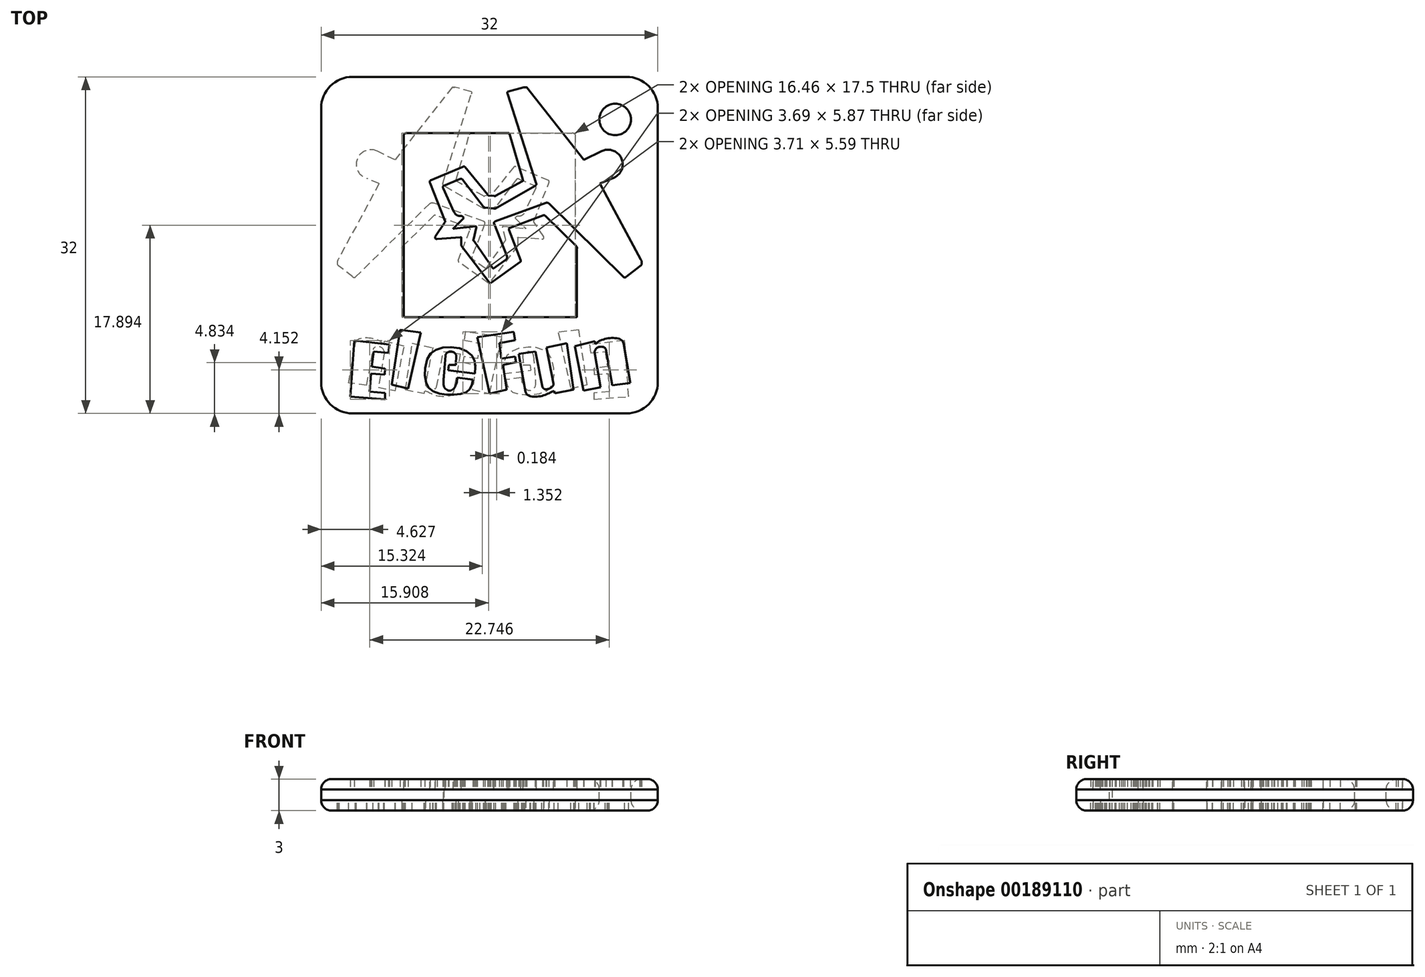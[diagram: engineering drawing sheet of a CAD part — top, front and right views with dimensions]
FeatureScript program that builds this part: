
annotation { "Feature Type Name" : "Feature", "Feature Type Description" : "" }
export const myFeature = defineFeature(function(context is Context, id is Id, definition is map)
    precondition{}
    {
        {
            var Q0;
            Q0=qCreatedBy(makeId("Top.planeOp"),FACE);
            var sketch = newSketch(context, id + "F0", { "sketchPlane" : qUnion([Q0])});
            skLineSegment(sketch, "E0", {"start": v(-15, 0) * mm, "end": v(15, 0) * mm, "construction": true});
            skLineSegment(sketch, "E1", {"start": v(0, 15) * mm, "end": v(0, 0) * mm, "construction": true});
            skLineSegment(sketch, "E2", {"start": v(0, 0) * mm, "end": v(0, -15) * mm, "construction": true});
            skLineSegment(sketch, "E3", {"start": v(1.86, 10.64) * mm, "end": v(-7.86, 10.64) * mm});
            skLineSegment(sketch, "E4", {"start": v(-8.14, 10.51) * mm, "end": v(-8.14, -6.7) * mm});
            skLineSegment(sketch, "E5", {"start": v(-8.02, -6.86) * mm, "end": v(8.23, -6.86) * mm});
            skLineSegment(sketch, "E6", {"start": v(8.32, -6.77) * mm, "end": v(8.32, -0.32) * mm});
            skLineSegment(sketch, "E7", {"start": v(8.28, -0.12) * mm, "end": v(5.28, 2.8) * mm});
            skLineSegment(sketch, "E8", {"start": v(1.92, 1.65) * mm, "end": v(5.12, 2.84) * mm});
            skLineSegment(sketch, "E9", {"start": v(1.74, 14.6) * mm, "end": v(3.24, 15) * mm});
            skLineSegment(sketch, "E10", {"start": v(3.55, 15) * mm, "end": v(8.98, 8.11) * mm});
            skLineSegment(sketch, "E11", {"start": v(8.98, 8.11) * mm, "end": v(10.65, 8.93) * mm});
            skLineSegment(sketch, "E12", {"start": v(10.49, 5.85) * mm, "end": v(11.64, 6.34) * mm});
            skLineSegment(sketch, "E13", {"start": v(10.49, 5.85) * mm, "end": v(14.37, -1.36) * mm});
            skLineSegment(sketch, "E14", {"start": v(13, -3.01) * mm, "end": v(14.27, -2.02) * mm});
            skLineSegment(sketch, "E15", {"start": v(12.74, -3.04) * mm, "end": v(5.65, 3.98) * mm});
            skLineSegment(sketch, "E16", {"start": v(0.54, 2.26) * mm, "end": v(5.35, 4.02) * mm});
            skLineSegment(sketch, "E17", {"start": v(0.45, 2.02) * mm, "end": v(1.66, -1.06) * mm});
            skLineSegment(sketch, "E18", {"start": v(2.97, -1.46) * mm, "end": v(1.87, 1.45) * mm});
            skLineSegment(sketch, "E19", {"start": v(0.4, -2.2) * mm, "end": v(1.6, -1.35) * mm});
            skLineSegment(sketch, "E20", {"start": v(0.28, -2.17) * mm, "end": v(-1.46, 0.35) * mm});
            skLineSegment(sketch, "E21", {"start": v(-1.52, 0.54) * mm, "end": v(-1.27, 1.67) * mm});
            skLineSegment(sketch, "E22", {"start": v(-1.33, 1.8) * mm, "end": v(-3.35, 1.58) * mm});
            skLineSegment(sketch, "E23", {"start": v(-2.43, 2.57) * mm, "end": v(-3.32, 1.7) * mm});
            skLineSegment(sketch, "E24", {"start": v(-2.43, 2.57) * mm, "end": v(-2.63, 2.76) * mm});
            skLineSegment(sketch, "E25", {"start": v(-4.4, 5.43) * mm, "end": v(-3.37, 3.16) * mm});
            skLineSegment(sketch, "E26", {"start": v(-2.79, 0.76) * mm, "end": v(-4.98, 0.6) * mm});
            skLineSegment(sketch, "E27", {"start": v(-5.16, 0.8) * mm, "end": v(-4.24, 2.18) * mm});
            skLineSegment(sketch, "E28", {"start": v(-4.24, 2.33) * mm, "end": v(-5.63, 5.88) * mm});
            skLineSegment(sketch, "E29", {"start": v(-5.63, 6.15) * mm, "end": v(-2.51, 7.46) * mm});
            skLineSegment(sketch, "E30", {"start": v(-2.34, 7.46) * mm, "end": v(-0.18, 4.8) * mm});
            skLineSegment(sketch, "E31", {"start": v(-0.07, 4.7) * mm, "end": v(0.46, 4.67) * mm});
            skLineSegment(sketch, "E32", {"start": v(0.57, 4.67) * mm, "end": v(3.12, 6.06) * mm});
            skLineSegment(sketch, "E33", {"start": v(3.16, 6.27) * mm, "end": v(1.9, 10.52) * mm});
            skLineSegment(sketch, "E34", {"start": v(0.1, -3.6) * mm, "end": v(2.9, -1.6) * mm});
            skLineSegment(sketch, "E35", {"start": v(-2.68, 0.7) * mm, "end": v(-2.7, 0.01) * mm});
            skLineSegment(sketch, "E36", {"start": v(-2.68, -0.05) * mm, "end": v(-0.03, -3.54) * mm});
            skLineSegment(sketch, "E37", {"start": v(-2.76, 6.3) * mm, "end": v(-4.36, 5.63) * mm});
            skLineSegment(sketch, "E38", {"start": v(-2.58, 6.26) * mm, "end": v(-0.6, 3.66) * mm});
            skLineSegment(sketch, "E39", {"start": v(-0.42, 3.58) * mm, "end": v(0.4, 3.49) * mm});
            skLineSegment(sketch, "E40", {"start": v(0.57, 3.49) * mm, "end": v(4.32, 5.63) * mm});
            skLineSegment(sketch, "E41", {"start": v(4.44, 5.9) * mm, "end": v(1.72, 14.38) * mm});
            skArc(sketch, "E42", {"start": v(11.64, 6.34) * mm, "mid": v(12.57, 8.18) * mm, "end": v(10.65, 8.93) * mm});
            skFitSpline(sketch, "E43", {"points": [v(1.74, 14.6) * mm, v(1.69, 14.5) * mm, v(1.72, 14.38) * mm], "startDerivative": vector(-0.14, -0.18) * mm, "endDerivative": vector(0.1, -0.25) * mm});
            skFitSpline(sketch, "E44", {"points": [v(3.24, 15) * mm, v(3.45, 15) * mm, v(3.55, 15) * mm], "startDerivative": vector(0.4, 0.05) * mm, "endDerivative": vector(0.21, -0.06) * mm});
            skFitSpline(sketch, "E45", {"points": [v(14.37, -1.36) * mm, v(14.45, -1.51) * mm, v(14.47, -1.68) * mm, v(14.44, -1.84) * mm, v(14.27, -2.02) * mm], "startDerivative": vector(0.37, -0.61) * mm, "endDerivative": vector(-0.7, -0.58) * mm});
            skFitSpline(sketch, "E46", {"points": [v(13, -3.01) * mm, v(12.88, -3.08) * mm, v(12.74, -3.04) * mm], "startDerivative": vector(-0.22, -0.18) * mm, "endDerivative": vector(-0.3, 0.12) * mm});
            skFitSpline(sketch, "E47", {"points": [v(5.65, 3.98) * mm, v(5.5, 4.03) * mm, v(5.35, 4.02) * mm], "startDerivative": vector(-0.3, 0.13) * mm, "endDerivative": vector(-0.3, -0.04) * mm});
            skArc(sketch, "E48", {"start": v(5.28, 2.8) * mm, "mid": v(5.2, 2.84) * mm, "end": v(5.12, 2.84) * mm});
            skFitSpline(sketch, "E49", {"points": [v(1.92, 1.65) * mm, v(1.86, 1.6) * mm, v(1.85, 1.55) * mm, v(1.87, 1.45) * mm], "startDerivative": vector(-0.21, -0.1) * mm, "endDerivative": vector(0.08, -0.26) * mm});
            skFitSpline(sketch, "E50", {"points": [v(2.97, -1.46) * mm, v(2.98, -1.5) * mm, v(2.97, -1.54) * mm, v(2.95, -1.57) * mm, v(2.9, -1.6) * mm], "startDerivative": vector(0.05, -0.15) * mm, "endDerivative": vector(-0.18, -0.1) * mm});
            skFitSpline(sketch, "E51", {"points": [v(1.66, -1.06) * mm, v(1.66, -1.2) * mm, v(1.6, -1.35) * mm], "startDerivative": vector(0.05, -0.3) * mm, "endDerivative": vector(-0.15, -0.27) * mm});
            skFitSpline(sketch, "E52", {"points": [v(0.4, -2.2) * mm, v(0.35, -2.2) * mm, v(0.28, -2.17) * mm], "startDerivative": vector(-0.13, -0.01) * mm, "endDerivative": vector(-0.12, 0.07) * mm});
            skArc(sketch, "E53", {"start": v(-1.52, 0.54) * mm, "mid": v(-1.52, 0.44) * mm, "end": v(-1.46, 0.35) * mm});
            skFitSpline(sketch, "E54", {"points": [v(-1.27, 1.67) * mm, v(-1.26, 1.7) * mm, v(-1.26, 1.75) * mm, v(-1.27, 1.77) * mm, v(-1.28, 1.79) * mm, v(-1.3, 1.8) * mm, v(-1.33, 1.8) * mm], "startDerivative": vector(0.06, 0.2) * mm, "endDerivative": vector(-0.18, -0.02) * mm});
            skFitSpline(sketch, "E55", {"points": [v(-3.32, 1.7) * mm, v(-3.4, 1.63) * mm, v(-3.44, 1.58) * mm, v(-3.43, 1.57) * mm, v(-3.4, 1.57) * mm, v(-3.35, 1.58) * mm], "startDerivative": vector(-0.28, -0.26) * mm, "endDerivative": vector(0.25, 0.03) * mm});
            skFitSpline(sketch, "E56", {"points": [v(-4.24, 2.18) * mm, v(-4.23, 2.2) * mm, v(-4.21, 2.23) * mm, v(-4.21, 2.25) * mm, v(-4.22, 2.28) * mm, v(-4.23, 2.31) * mm, v(-4.24, 2.33) * mm], "startDerivative": vector(0.05, 0.12) * mm, "endDerivative": vector(-0.05, 0.14) * mm});
            skFitSpline(sketch, "E57", {"points": [v(-2.63, 2.76) * mm, v(-2.75, 2.76) * mm, v(-2.87, 2.76) * mm, v(-3, 2.8) * mm, v(-3.15, 2.89) * mm, v(-3.26, 3) * mm, v(-3.37, 3.16) * mm], "startDerivative": vector(-0.82, 0.01) * mm, "endDerivative": vector(-0.6, 0.94) * mm});
            skFitSpline(sketch, "E58", {"points": [v(-4.4, 5.43) * mm, v(-4.44, 5.55) * mm, v(-4.36, 5.63) * mm], "startDerivative": vector(-0.14, 0.26) * mm, "endDerivative": vector(0.23, 0.16) * mm});
            skFitSpline(sketch, "E59", {"points": [v(-2.76, 6.3) * mm, v(-2.66, 6.3) * mm, v(-2.58, 6.26) * mm], "startDerivative": vector(0.22, 0.03) * mm, "endDerivative": vector(0.16, -0.12) * mm});
            skFitSpline(sketch, "E60", {"points": [v(-0.6, 3.66) * mm, v(-0.52, 3.6) * mm, v(-0.42, 3.58) * mm], "startDerivative": vector(0.15, -0.13) * mm, "endDerivative": vector(0.2, -0.02) * mm});
            skFitSpline(sketch, "E61", {"points": [v(0.4, 3.49) * mm, v(0.5, 3.49) * mm, v(0.57, 3.49) * mm], "startDerivative": vector(0.17, 0) * mm, "endDerivative": vector(0.15, 0) * mm});
            skFitSpline(sketch, "E62", {"points": [v(0.57, 4.67) * mm, v(0.54, 4.66) * mm, v(0.46, 4.67) * mm], "startDerivative": vector(-0.06, -0.02) * mm, "endDerivative": vector(-0.15, 0.02) * mm});
            skFitSpline(sketch, "E63", {"points": [v(-0.07, 4.7) * mm, v(-0.12, 4.73) * mm, v(-0.18, 4.8) * mm], "startDerivative": vector(-0.12, 0.05) * mm, "endDerivative": vector(-0.1, 0.13) * mm});
            skFitSpline(sketch, "E64", {"points": [v(-8.14, 10.51) * mm, v(-8.07, 10.6) * mm, v(-7.95, 10.64) * mm, v(-7.86, 10.64) * mm], "startDerivative": vector(0.18, 0.27) * mm, "endDerivative": vector(0.29, 0) * mm});
            skFitSpline(sketch, "E65", {"points": [v(1.9, 10.52) * mm, v(1.88, 10.6) * mm, v(1.86, 10.64) * mm], "startDerivative": vector(-0.05, 0.15) * mm, "endDerivative": vector(-0.04, 0.1) * mm});
            skFitSpline(sketch, "E66", {"points": [v(4.44, 5.9) * mm, v(4.45, 5.84) * mm, v(4.45, 5.77) * mm, v(4.43, 5.72) * mm, v(4.4, 5.69) * mm, v(4.32, 5.63) * mm], "startDerivative": vector(0.07, -0.32) * mm, "endDerivative": vector(-0.37, -0.23) * mm});
            skFitSpline(sketch, "E67", {"points": [v(3.12, 6.06) * mm, v(3.16, 6.1) * mm, v(3.18, 6.13) * mm, v(3.18, 6.17) * mm, v(3.16, 6.27) * mm], "startDerivative": vector(0.2, 0.13) * mm, "endDerivative": vector(-0.1, 0.32) * mm});
            skFitSpline(sketch, "E68", {"points": [v(-4.98, 0.6) * mm, v(-5.04, 0.6) * mm, v(-5.1, 0.6) * mm, v(-5.13, 0.63) * mm, v(-5.16, 0.66) * mm, v(-5.17, 0.7) * mm, v(-5.17, 0.74) * mm, v(-5.17, 0.78) * mm, v(-5.16, 0.8) * mm], "startDerivative": vector(-0.4, 0) * mm, "endDerivative": vector(0.04, 0.24) * mm});
            skFitSpline(sketch, "E69", {"points": [v(-2.68, 0.7) * mm, v(-2.68, 0.73) * mm, v(-2.69, 0.74) * mm, v(-2.7, 0.75) * mm, v(-2.72, 0.76) * mm, v(-2.74, 0.76) * mm, v(-2.79, 0.76) * mm], "startDerivative": vector(-0.02, 0.12) * mm, "endDerivative": vector(-0.22, -0.02) * mm});
            skFitSpline(sketch, "E70", {"points": [v(-2.68, -0.05) * mm, v(-2.7, -0.03) * mm, v(-2.7, 0.01) * mm], "startDerivative": vector(-0.02, 0.05) * mm, "endDerivative": vector(0, 0.08) * mm});
            skFitSpline(sketch, "E71", {"points": [v(0.1, -3.6) * mm, v(0.08, -3.6) * mm, v(0.04, -3.6) * mm, v(0, -3.6) * mm, v(-0.03, -3.54) * mm], "startDerivative": vector(-0.1, -0.1) * mm, "endDerivative": vector(-0.12, 0.19) * mm});
            skFitSpline(sketch, "E72", {"points": [v(-8.14, -6.7) * mm, v(-8.14, -6.74) * mm, v(-8.13, -6.78) * mm, v(-8.1, -6.82) * mm, v(-8.08, -6.84) * mm, v(-8.04, -6.86) * mm, v(-8.02, -6.86) * mm], "startDerivative": vector(-0.01, -0.18) * mm, "endDerivative": vector(0.15, 0.01) * mm});
            skFitSpline(sketch, "E73", {"points": [v(8.32, -6.77) * mm, v(8.3, -6.83) * mm, v(8.23, -6.86) * mm], "startDerivative": vector(-0.01, -0.15) * mm, "endDerivative": vector(-0.16, -0.02) * mm});
            skFitSpline(sketch, "E74", {"points": [v(8.32, -0.32) * mm, v(8.32, -0.22) * mm, v(8.28, -0.12) * mm], "startDerivative": vector(0.02, 0.2) * mm, "endDerivative": vector(-0.1, 0.2) * mm});
            skFitSpline(sketch, "E75", {"points": [v(-5.63, 5.88) * mm, v(-5.68, 6.02) * mm, v(-5.63, 6.15) * mm], "startDerivative": vector(-0.15, 0.28) * mm, "endDerivative": vector(0.15, 0.27) * mm});
            skFitSpline(sketch, "E76", {"points": [v(-2.51, 7.46) * mm, v(-2.42, 7.48) * mm, v(-2.34, 7.46) * mm], "startDerivative": vector(0.18, 0.06) * mm, "endDerivative": vector(0.15, -0.07) * mm});
            skLineSegment(sketch, "E77", {"start": v(-9.52, -9.44) * mm, "end": v(-9.6, -10.25) * mm});
            skLineSegment(sketch, "E78", {"start": v(-9.6, -10.25) * mm, "end": v(-11, -10.11) * mm});
            skLineSegment(sketch, "E79", {"start": v(-11, -10.11) * mm, "end": v(-11.2, -11.55) * mm});
            skLineSegment(sketch, "E80", {"start": v(-11.2, -11.55) * mm, "end": v(-9.91, -11.72) * mm});
            skLineSegment(sketch, "E81", {"start": v(-9.91, -11.72) * mm, "end": v(-9.96, -12.3) * mm});
            skLineSegment(sketch, "E82", {"start": v(-9.96, -12.3) * mm, "end": v(-11.25, -12.2) * mm});
            skLineSegment(sketch, "E83", {"start": v(-11.25, -12.2) * mm, "end": v(-11.4, -13.92) * mm});
            skLineSegment(sketch, "E84", {"start": v(-11.4, -13.92) * mm, "end": v(-9.9, -14.05) * mm});
            skLineSegment(sketch, "E85", {"start": v(-9.9, -14.05) * mm, "end": v(-9.9, -14.64) * mm});
            skLineSegment(sketch, "E86", {"start": v(-9.9, -14.64) * mm, "end": v(-13.23, -14.4) * mm});
            skLineSegment(sketch, "E87", {"start": v(-13.23, -14.4) * mm, "end": v(-12.84, -9.05) * mm});
            skLineSegment(sketch, "E88", {"start": v(-12.84, -9.05) * mm, "end": v(-9.52, -9.44) * mm});
            skLineSegment(sketch, "E89", {"start": v(-8.48, -8.05) * mm, "end": v(-6.54, -8.29) * mm});
            skLineSegment(sketch, "E90", {"start": v(-6.54, -8.29) * mm, "end": v(-7.72, -13.63) * mm});
            skLineSegment(sketch, "E91", {"start": v(-7.72, -13.63) * mm, "end": v(-9.28, -13.26) * mm});
            skLineSegment(sketch, "E92", {"start": v(-9.28, -13.26) * mm, "end": v(-8.48, -8.05) * mm});
            skLineSegment(sketch, "E93", {"start": v(-3.17, -10.43) * mm, "end": v(-3.2, -11.4) * mm});
            skLineSegment(sketch, "E94", {"start": v(-3.2, -11.4) * mm, "end": v(-3.87, -11.4) * mm});
            skFitSpline(sketch, "E95", {"points": [v(-4.2, -10.53) * mm, v(-4.15, -10.37) * mm, v(-4.02, -10.22) * mm, v(-3.84, -10.13) * mm, v(-3.58, -10.13) * mm, v(-3.37, -10.2) * mm, v(-3.24, -10.32) * mm, v(-3.17, -10.43) * mm], "startDerivative": vector(0.24, 1.24) * mm, "endDerivative": vector(0.53, -0.96) * mm});
            skLineSegment(sketch, "E96", {"start": v(-1.38, -12.22) * mm, "end": v(-3.93, -11.9) * mm});
            skLineSegment(sketch, "E97", {"start": v(-3.06, -12.6) * mm, "end": v(-1.58, -12.8) * mm});
            skFitSpline(sketch, "E98", {"points": [v(-1.58, -12.8) * mm, v(-1.61, -13.06) * mm, v(-1.68, -13.28) * mm, v(-1.78, -13.5) * mm, v(-1.9, -13.7) * mm, v(-2.08, -13.9) * mm, v(-2.35, -14.05) * mm, v(-2.72, -14.14) * mm, v(-3.17, -14.2) * mm, v(-3.7, -14.2) * mm, v(-4.27, -14.19) * mm, v(-4.76, -14.11) * mm, v(-5.25, -13.94) * mm, v(-5.5, -13.78) * mm, v(-5.75, -13.59) * mm, v(-5.94, -13.25) * mm, v(-6.09, -12.8) * mm, v(-6.14, -12.22) * mm, v(-6.12, -11.7) * mm, v(-5.92, -10.84) * mm, v(-5.69, -10.42) * mm, v(-5.37, -10.12) * mm, v(-4.96, -9.9) * mm, v(-4.42, -9.73) * mm, v(-3.73, -9.7) * mm, v(-2.96, -9.77) * mm, v(-2.33, -9.98) * mm, v(-1.87, -10.28) * mm, v(-1.58, -10.62) * mm, v(-1.4, -10.98) * mm, v(-1.35, -11.33) * mm, v(-1.34, -11.71) * mm, v(-1.38, -12.22) * mm], "startDerivative": vector(-0.95, -11.32) * mm, "endDerivative": vector(-1.59, -15.64) * mm});
            skLineSegment(sketch, "E99", {"start": v(1.62, -13.75) * mm, "end": v(0, -14.1) * mm});
            skLineSegment(sketch, "E100", {"start": v(0, -14.1) * mm, "end": v(-1.17, -8.73) * mm});
            skLineSegment(sketch, "E101", {"start": v(-1.17, -8.73) * mm, "end": v(2.3, -8.23) * mm});
            skLineSegment(sketch, "E102", {"start": v(2.3, -8.23) * mm, "end": v(2.42, -9.03) * mm});
            skLineSegment(sketch, "E103", {"start": v(2.42, -9.03) * mm, "end": v(0.92, -9.32) * mm});
            skLineSegment(sketch, "E104", {"start": v(0.92, -9.32) * mm, "end": v(1.14, -10.78) * mm});
            skLineSegment(sketch, "E105", {"start": v(1.14, -10.78) * mm, "end": v(2.44, -10.6) * mm});
            skLineSegment(sketch, "E106", {"start": v(2.44, -10.6) * mm, "end": v(2.52, -11.14) * mm});
            skLineSegment(sketch, "E107", {"start": v(2.52, -11.14) * mm, "end": v(1.28, -11.38) * mm});
            skLineSegment(sketch, "E108", {"start": v(1.28, -11.38) * mm, "end": v(1.62, -13.75) * mm});
            skLineSegment(sketch, "E109", {"start": v(7.98, -13.75) * mm, "end": v(6.2, -14.08) * mm});
            skLineSegment(sketch, "E110", {"start": v(6.2, -14.08) * mm, "end": v(6.13, -13.86) * mm});
            skLineSegment(sketch, "E111", {"start": v(7.98, -13.75) * mm, "end": v(7.34, -9.32) * mm});
            skLineSegment(sketch, "E112", {"start": v(7.34, -9.32) * mm, "end": v(5.4, -9.74) * mm});
            skLineSegment(sketch, "E113", {"start": v(5.4, -9.74) * mm, "end": v(6.08, -13.15) * mm});
            skLineSegment(sketch, "E114", {"start": v(5.02, -13.5) * mm, "end": v(4.37, -10.12) * mm});
            skLineSegment(sketch, "E115", {"start": v(4.37, -10.12) * mm, "end": v(2.77, -10.33) * mm});
            skLineSegment(sketch, "E116", {"start": v(2.77, -10.33) * mm, "end": v(3.4, -13.9) * mm});
            skFitSpline(sketch, "E117", {"points": [v(3.4, -13.9) * mm, v(3.49, -14.1) * mm, v(3.68, -14.27) * mm, v(3.94, -14.38) * mm, v(4.27, -14.4) * mm, v(4.69, -14.38) * mm, v(5.07, -14.3) * mm, v(5.38, -14.2) * mm, v(5.68, -14.07) * mm, v(5.87, -13.97) * mm, v(6, -13.9) * mm, v(6.13, -13.86) * mm], "startDerivative": vector(0.77, -2.56) * mm, "endDerivative": vector(2.11, 0.24) * mm});
            skFitSpline(sketch, "E118", {"points": [v(6.08, -13.15) * mm, v(6.08, -13.3) * mm, v(5.99, -13.43) * mm, v(5.86, -13.54) * mm, v(5.67, -13.64) * mm, v(5.51, -13.68) * mm, v(5.33, -13.7) * mm, v(5.2, -13.66) * mm, v(5.11, -13.6) * mm, v(5.02, -13.5) * mm], "startDerivative": vector(0.2, -1.45) * mm, "endDerivative": vector(-0.8, 1.2) * mm});
            skLineSegment(sketch, "E119", {"start": v(10.55, -13.52) * mm, "end": v(8.95, -13.82) * mm});
            skLineSegment(sketch, "E120", {"start": v(8.95, -13.82) * mm, "end": v(8.1, -9.6) * mm});
            skLineSegment(sketch, "E121", {"start": v(8.1, -9.6) * mm, "end": v(10.02, -9.13) * mm});
            skLineSegment(sketch, "E122", {"start": v(10.02, -9.13) * mm, "end": v(10.05, -9.43) * mm});
            skLineSegment(sketch, "E123", {"start": v(9.98, -10.17) * mm, "end": v(10.55, -13.52) * mm});
            skLineSegment(sketch, "E124", {"start": v(11.66, -13.3) * mm, "end": v(11.06, -9.93) * mm});
            skLineSegment(sketch, "E125", {"start": v(11.66, -13.3) * mm, "end": v(13.38, -13.1) * mm});
            skLineSegment(sketch, "E126", {"start": v(13.38, -13.1) * mm, "end": v(12.75, -9.36) * mm});
            skPoint(sketch, "E127.1.internal.snap0", {"position": v(10.04, -9.28) * mm});
            skFitSpline(sketch, "E127", {"points": [v(9.98, -10.17) * mm, v(10.04, -9.98) * mm, v(10.15, -9.81) * mm, v(10.35, -9.7) * mm, v(10.58, -9.65) * mm, v(10.8, -9.68) * mm, v(10.92, -9.73) * mm, v(11, -9.8) * mm, v(11.06, -9.93) * mm], "startDerivative": vector(0.35, 1.5) * mm, "endDerivative": vector(0.4, -1.27) * mm});
            skFitSpline(sketch, "E128", {"points": [v(10.05, -9.43) * mm, v(10.22, -9.26) * mm, v(10.4, -9.14) * mm, v(10.7, -9) * mm, v(11.1, -8.88) * mm, v(11.5, -8.83) * mm, v(11.9, -8.84) * mm, v(12.26, -8.88) * mm, v(12.5, -8.98) * mm, v(12.65, -9.13) * mm, v(12.7, -9.24) * mm, v(12.75, -9.36) * mm], "startDerivative": vector(2, 2.1) * mm, "endDerivative": vector(0.8, -1.94) * mm});
            skFitSpline(sketch, "E129", {"points": [v(-4.1, -11.87) * mm, v(-4.2, -12.04) * mm, v(-4.27, -12.28) * mm, v(-4.35, -12.58) * mm, v(-4.37, -12.86) * mm, v(-4.38, -13.16) * mm, v(-4.32, -13.48) * mm, v(-4.14, -13.7) * mm, v(-3.92, -13.8) * mm, v(-3.7, -13.82) * mm, v(-3.5, -13.73) * mm, v(-3.35, -13.58) * mm, v(-3.22, -13.37) * mm, v(-3.14, -13.13) * mm, v(-3.1, -12.91) * mm, v(-3.06, -12.6) * mm], "startDerivative": vector(-1.74, -2.77) * mm, "endDerivative": vector(0.4, 4.42) * mm});
            skFitSpline(sketch, "E130", {"points": [v(0.45, 2.02) * mm, v(0.43, 2.1) * mm, v(0.45, 2.18) * mm, v(0.54, 2.26) * mm], "startDerivative": vector(-0.1, 0.25) * mm, "endDerivative": vector(0.3, 0.19) * mm});
            skLineSegment(sketch, "E131", {"start": v(8.89, 15) * mm, "end": v(15, 8.89) * mm, "construction": true});
            skCircle(sketch, "E132", {"center": v(11.94, 11.94) * mm, "radius": 1.5 * mm});
            skLineSegment(sketch, "E133.bottom", {"start": v(-13, 16) * mm, "end": v(13, 16) * mm});
            skLineSegment(sketch, "E133.top", {"start": v(-13, -16) * mm, "end": v(13, -16) * mm});
            skLineSegment(sketch, "E133.left", {"start": v(-16, 13) * mm, "end": v(-16, -13) * mm});
            skLineSegment(sketch, "E133.right", {"start": v(16, 13) * mm, "end": v(16, -13) * mm});
            skLineSegment(sketch, "E134", {"start": v(-16, 0) * mm, "end": v(16, 0) * mm, "construction": true});
            skLineSegment(sketch, "E135", {"start": v(0, 16) * mm, "end": v(0, -16) * mm, "construction": true});
            skLineSegment(sketch, "E136", {"start": v(0, 0) * mm, "end": v(0, -16) * mm, "construction": true});
            skLineSegment(sketch, "E137", {"start": v(0, -16) * mm, "end": v(0, 0) * mm, "construction": true});
            skLineSegment(sketch, "E138", {"start": v(0, 16) * mm, "end": v(0, 0) * mm, "construction": true});
            skPoint(sketch, "E139.visualSharp", {"position": v(-16, 16) * mm});
            skArc(sketch, "E139.filletArc", {"start": v(-13, 16) * mm, "mid": v(-15.12, 15.12) * mm, "end": v(-16, 13) * mm});
            skPoint(sketch, "E140.visualSharp", {"position": v(16, 16) * mm});
            skArc(sketch, "E140.filletArc", {"start": v(16, 13) * mm, "mid": v(15.12, 15.12) * mm, "end": v(13, 16) * mm});
            skPoint(sketch, "E141.visualSharp", {"position": v(16, -16) * mm});
            skArc(sketch, "E141.filletArc", {"start": v(13, -16) * mm, "mid": v(15.12, -15.12) * mm, "end": v(16, -13) * mm});
            skPoint(sketch, "E142.visualSharp", {"position": v(-16, -16) * mm});
            skArc(sketch, "E142.filletArc", {"start": v(-16, -13) * mm, "mid": v(-15.12, -15.12) * mm, "end": v(-13, -16) * mm});
            skLineSegment(sketch, "E143", {"start": v(-4.19, -10.48) * mm, "end": v(-4.37, -12.86) * mm});
            skLineSegment(sketch, "E144", {"start": v(-3.87, -11.4) * mm, "end": v(-3.93, -11.9) * mm});
            skSolve(sketch);
        }
        {
            var Q0;
            Q0=makeQuery(id+"F0.imprint","IMPRINT",FACE,{"disambiguationData":[TD([[makeQuery(id+"F0.imprint","IMPRINT",EDGE,{"derivedFrom":sQuery(id+"F0.wireOp",EDGE,"E9")}),-1.0]])]});
            var Q1;
            Q1=makeQuery(id+"F0.imprint","IMPRINT",FACE,{"disambiguationData":[TD([[makeQuery(id+"F0.imprint","IMPRINT",EDGE,{"derivedFrom":sQuery(id+"F0.wireOp",EDGE,"E132")}),1.0]])]});
            var Q2;
            Q2=makeQuery(id+"F0.imprint","IMPRINT",FACE,{"disambiguationData":[TD([[makeQuery(id+"F0.imprint","IMPRINT",EDGE,{"derivedFrom":sQuery(id+"F0.wireOp",EDGE,"E119")}),-1.0]])]});
            var Q3;
            Q3=makeQuery(id+"F0.imprint","IMPRINT",FACE,{"disambiguationData":[TD([[makeQuery(id+"F0.imprint","IMPRINT",EDGE,{"derivedFrom":sQuery(id+"F0.wireOp",EDGE,"E93")}),1.0]])]});
            var Q4;
            Q4=makeQuery(id+"F0.imprint","IMPRINT",FACE,{"disambiguationData":[TD([[makeQuery(id+"F0.imprint","IMPRINT",EDGE,{"derivedFrom":sQuery(id+"F0.wireOp",EDGE,"E3")}),1.0]])]});
            var Q5;
            Q5=makeQuery(id+"F0.imprint","IMPRINT",FACE,{"disambiguationData":[TD([[makeQuery(id+"F0.imprint","IMPRINT",EDGE,{"derivedFrom":sQuery(id+"F0.wireOp",EDGE,"E3")}),-1.0]])]});
            var Q6;
            Q6=makeQuery(id+"F0.imprint","IMPRINT",FACE,{"disambiguationData":[TD([[makeQuery(id+"F0.imprint","IMPRINT",EDGE,{"derivedFrom":sQuery(id+"F0.wireOp",EDGE,"E89")}),-1.0]])]});
            var Q7;
            Q7=makeQuery(id+"F0.imprint","IMPRINT",FACE,{"disambiguationData":[TD([[makeQuery(id+"F0.imprint","IMPRINT",EDGE,{"derivedFrom":sQuery(id+"F0.wireOp",EDGE,"E99")}),-1.0]])]});
            var Q8;
            Q8=makeQuery(id+"F0.imprint","IMPRINT",FACE,{"disambiguationData":[TD([[makeQuery(id+"F0.imprint","IMPRINT",EDGE,{"derivedFrom":sQuery(id+"F0.wireOp",EDGE,"E109")}),-1.0]])]});
            var Q9;
            Q9=makeQuery(id+"F0.imprint","IMPRINT",FACE,{"disambiguationData":[TD([[makeQuery(id+"F0.imprint","IMPRINT",EDGE,{"derivedFrom":sQuery(id+"F0.wireOp",EDGE,"E77")}),-1.0]])]});
            extrude(context, id + "F1", {"entities" : qUnion([Q0, Q1, Q2, Q3, Q4, Q5, Q6, Q7, Q8, Q9]), "oppositeDirection" : true, "depth" : 1 * mm});
        }
        {
            var Q0;
            Q0=makeQuery(id+"F0.imprint","IMPRINT",FACE,{"disambiguationData":[TD([[makeQuery(id+"F0.imprint","IMPRINT",EDGE,{"derivedFrom":sQuery(id+"F0.wireOp",EDGE,"E3")}),-1.0]])]});
            extrude(context, id + "F2", {"entities" : qUnion([Q0]), "depth" : 1 * mm});
        }
        {
            var Q0;
            Q0=makeQuery(id+"F1.opExtrude","CAP_FACE",FACE,{"disambiguationData":[OSD([sQuery(id+"F0.wireOp",EDGE,"E133.bottom"),sQuery(id+"F0.wireOp",EDGE,"E133.top"),sQuery(id+"F0.wireOp",EDGE,"E133.left"),sQuery(id+"F0.wireOp",EDGE,"E133.right"),sQuery(id+"F0.wireOp",EDGE,"E139.filletArc"),sQuery(id+"F0.wireOp",EDGE,"E140.filletArc"),sQuery(id+"F0.wireOp",EDGE,"E141.filletArc"),sQuery(id+"F0.wireOp",EDGE,"E142.filletArc")])],"isStart":false});
            var sketch = newSketch(context, id + "F3", { "sketchPlane" : qUnion([Q0])});
            skLineSegment(sketch, "E145", {"start": v(-15.73, 2.68) * mm, "end": v(14.27, 2.68) * mm, "construction": true});
            skLineSegment(sketch, "E146", {"start": v(-0.73, 17.68) * mm, "end": v(-0.73, 2.68) * mm, "construction": true});
            skLineSegment(sketch, "E147", {"start": v(-0.73, 2.68) * mm, "end": v(-0.73, -12.32) * mm, "construction": true});
            skLineSegment(sketch, "E148", {"start": v(1.13, 13.33) * mm, "end": v(-8.59, 13.33) * mm});
            skLineSegment(sketch, "E149", {"start": v(-8.87, 13.2) * mm, "end": v(-8.87, -4.03) * mm});
            skLineSegment(sketch, "E150", {"start": v(-8.75, -4.17) * mm, "end": v(7.5, -4.17) * mm});
            skLineSegment(sketch, "E151", {"start": v(7.58, -4.09) * mm, "end": v(7.58, 2.37) * mm});
            skLineSegment(sketch, "E152", {"start": v(7.54, 2.56) * mm, "end": v(4.54, 5.48) * mm});
            skLineSegment(sketch, "E153", {"start": v(1.19, 4.33) * mm, "end": v(4.4, 5.53) * mm});
            skLineSegment(sketch, "E154", {"start": v(1, 17.28) * mm, "end": v(2.5, 17.67) * mm});
            skLineSegment(sketch, "E155", {"start": v(2.82, 17.67) * mm, "end": v(8.25, 10.8) * mm});
            skLineSegment(sketch, "E156", {"start": v(8.25, 10.8) * mm, "end": v(9.91, 11.61) * mm});
            skLineSegment(sketch, "E157", {"start": v(9.75, 8.54) * mm, "end": v(10.9, 9.02) * mm});
            skLineSegment(sketch, "E158", {"start": v(9.75, 8.54) * mm, "end": v(13.64, 1.32) * mm});
            skLineSegment(sketch, "E159", {"start": v(12.27, -0.33) * mm, "end": v(13.54, 0.67) * mm});
            skLineSegment(sketch, "E160", {"start": v(12, -0.36) * mm, "end": v(4.92, 6.66) * mm});
            skLineSegment(sketch, "E161", {"start": v(-0.19, 4.94) * mm, "end": v(4.62, 6.7) * mm});
            skLineSegment(sketch, "E162", {"start": v(-0.28, 4.7) * mm, "end": v(0.92, 1.62) * mm});
            skLineSegment(sketch, "E163", {"start": v(2.24, 1.22) * mm, "end": v(1.13, 4.14) * mm});
            skLineSegment(sketch, "E164", {"start": v(-0.33, 0.48) * mm, "end": v(0.87, 1.33) * mm});
            skLineSegment(sketch, "E165", {"start": v(-0.45, 0.51) * mm, "end": v(-2.2, 3.04) * mm});
            skLineSegment(sketch, "E166", {"start": v(-2.26, 3.23) * mm, "end": v(-2, 4.35) * mm});
            skLineSegment(sketch, "E167", {"start": v(-2.06, 4.48) * mm, "end": v(-4.08, 4.26) * mm});
            skLineSegment(sketch, "E168", {"start": v(-3.16, 5.25) * mm, "end": v(-4.06, 4.39) * mm});
            skLineSegment(sketch, "E169", {"start": v(-3.16, 5.25) * mm, "end": v(-3.36, 5.45) * mm});
            skLineSegment(sketch, "E170", {"start": v(-5.13, 8.1) * mm, "end": v(-4.1, 5.85) * mm});
            skLineSegment(sketch, "E171", {"start": v(-3.52, 3.44) * mm, "end": v(-5.71, 3.28) * mm});
            skLineSegment(sketch, "E172", {"start": v(-5.9, 3.48) * mm, "end": v(-4.97, 4.86) * mm});
            skLineSegment(sketch, "E173", {"start": v(-4.97, 5.02) * mm, "end": v(-6.36, 8.56) * mm});
            skLineSegment(sketch, "E174", {"start": v(-6.36, 8.84) * mm, "end": v(-3.24, 10.14) * mm});
            skLineSegment(sketch, "E175", {"start": v(-3.08, 10.14) * mm, "end": v(-0.91, 7.48) * mm});
            skLineSegment(sketch, "E176", {"start": v(-0.8, 7.39) * mm, "end": v(-0.27, 7.35) * mm});
            skLineSegment(sketch, "E177", {"start": v(-0.16, 7.35) * mm, "end": v(2.39, 8.75) * mm});
            skLineSegment(sketch, "E178", {"start": v(2.43, 8.95) * mm, "end": v(1.18, 13.2) * mm});
            skLineSegment(sketch, "E179", {"start": v(-0.63, -0.9) * mm, "end": v(2.17, 1.08) * mm});
            skLineSegment(sketch, "E180", {"start": v(-3.4, 3.4) * mm, "end": v(-3.42, 2.7) * mm});
            skLineSegment(sketch, "E181", {"start": v(-3.42, 2.63) * mm, "end": v(-0.76, -0.86) * mm});
            skLineSegment(sketch, "E182", {"start": v(-3.5, 8.99) * mm, "end": v(-5.09, 8.32) * mm});
            skLineSegment(sketch, "E183", {"start": v(-3.3, 8.94) * mm, "end": v(-1.33, 6.34) * mm});
            skLineSegment(sketch, "E184", {"start": v(-1.15, 6.26) * mm, "end": v(-0.32, 6.17) * mm});
            skLineSegment(sketch, "E185", {"start": v(-0.16, 6.17) * mm, "end": v(3.59, 8.32) * mm});
            skLineSegment(sketch, "E186", {"start": v(3.7, 8.58) * mm, "end": v(0.99, 17.06) * mm});
            skArc(sketch, "E187", {"start": v(10.9, 9.02) * mm, "mid": v(11.84, 10.86) * mm, "end": v(9.91, 11.61) * mm});
            skFitSpline(sketch, "E188", {"points": [v(1, 17.28) * mm, v(0.96, 17.19) * mm, v(0.99, 17.06) * mm], "startDerivative": vector(-0.14, -0.18) * mm, "endDerivative": vector(0.1, -0.25) * mm});
            skFitSpline(sketch, "E189", {"points": [v(2.5, 17.67) * mm, v(2.72, 17.7) * mm, v(2.82, 17.67) * mm], "startDerivative": vector(0.4, 0.05) * mm, "endDerivative": vector(0.21, -0.06) * mm});
            skFitSpline(sketch, "E190", {"points": [v(13.64, 1.32) * mm, v(13.72, 1.17) * mm, v(13.74, 1) * mm, v(13.71, 0.84) * mm, v(13.54, 0.67) * mm], "startDerivative": vector(0.37, -0.61) * mm, "endDerivative": vector(-0.7, -0.58) * mm});
            skFitSpline(sketch, "E191", {"points": [v(12.27, -0.33) * mm, v(12.15, -0.4) * mm, v(12, -0.36) * mm], "startDerivative": vector(-0.22, -0.18) * mm, "endDerivative": vector(-0.3, 0.12) * mm});
            skFitSpline(sketch, "E192", {"points": [v(4.92, 6.66) * mm, v(4.77, 6.71) * mm, v(4.62, 6.7) * mm], "startDerivative": vector(-0.3, 0.13) * mm, "endDerivative": vector(-0.3, -0.04) * mm});
            skArc(sketch, "E193", {"start": v(4.54, 5.48) * mm, "mid": v(4.47, 5.52) * mm, "end": v(4.4, 5.53) * mm});
            skFitSpline(sketch, "E194", {"points": [v(1.19, 4.33) * mm, v(1.13, 4.3) * mm, v(1.11, 4.23) * mm, v(1.13, 4.14) * mm], "startDerivative": vector(-0.21, -0.1) * mm, "endDerivative": vector(0.08, -0.26) * mm});
            skFitSpline(sketch, "E195", {"points": [v(2.24, 1.22) * mm, v(2.25, 1.19) * mm, v(2.24, 1.15) * mm, v(2.22, 1.1) * mm, v(2.17, 1.08) * mm], "startDerivative": vector(0.05, -0.15) * mm, "endDerivative": vector(-0.18, -0.1) * mm});
            skFitSpline(sketch, "E196", {"points": [v(0.92, 1.62) * mm, v(0.93, 1.47) * mm, v(0.87, 1.33) * mm], "startDerivative": vector(0.05, -0.3) * mm, "endDerivative": vector(-0.15, -0.27) * mm});
            skFitSpline(sketch, "E197", {"points": [v(-0.33, 0.48) * mm, v(-0.39, 0.48) * mm, v(-0.45, 0.51) * mm], "startDerivative": vector(-0.13, -0.01) * mm, "endDerivative": vector(-0.12, 0.07) * mm});
            skArc(sketch, "E198", {"start": v(-2.26, 3.23) * mm, "mid": v(-2.25, 3.12) * mm, "end": v(-2.2, 3.04) * mm});
            skFitSpline(sketch, "E199", {"points": [v(-2, 4.35) * mm, v(-2, 4.4) * mm, v(-2, 4.43) * mm, v(-2, 4.45) * mm, v(-2.01, 4.47) * mm, v(-2.03, 4.48) * mm, v(-2.06, 4.48) * mm], "startDerivative": vector(0.06, 0.2) * mm, "endDerivative": vector(-0.18, -0.02) * mm});
            skFitSpline(sketch, "E200", {"points": [v(-4.06, 4.39) * mm, v(-4.14, 4.31) * mm, v(-4.17, 4.27) * mm, v(-4.16, 4.25) * mm, v(-4.13, 4.25) * mm, v(-4.08, 4.26) * mm], "startDerivative": vector(-0.28, -0.26) * mm, "endDerivative": vector(0.25, 0.03) * mm});
            skFitSpline(sketch, "E201", {"points": [v(-4.97, 4.86) * mm, v(-4.96, 4.88) * mm, v(-4.95, 4.9) * mm, v(-4.95, 4.93) * mm, v(-4.95, 4.97) * mm, v(-4.96, 5) * mm, v(-4.97, 5.02) * mm], "startDerivative": vector(0.05, 0.12) * mm, "endDerivative": vector(-0.05, 0.14) * mm});
            skFitSpline(sketch, "E202", {"points": [v(-3.36, 5.45) * mm, v(-3.48, 5.45) * mm, v(-3.6, 5.45) * mm, v(-3.73, 5.49) * mm, v(-3.88, 5.57) * mm, v(-4, 5.67) * mm, v(-4.1, 5.85) * mm], "startDerivative": vector(-0.82, 0.01) * mm, "endDerivative": vector(-0.6, 0.94) * mm});
            skFitSpline(sketch, "E203", {"points": [v(-5.13, 8.1) * mm, v(-5.17, 8.23) * mm, v(-5.09, 8.32) * mm], "startDerivative": vector(-0.14, 0.26) * mm, "endDerivative": vector(0.23, 0.16) * mm});
            skFitSpline(sketch, "E204", {"points": [v(-3.5, 8.99) * mm, v(-3.39, 8.99) * mm, v(-3.3, 8.94) * mm], "startDerivative": vector(0.22, 0.03) * mm, "endDerivative": vector(0.16, -0.12) * mm});
            skFitSpline(sketch, "E205", {"points": [v(-1.33, 6.34) * mm, v(-1.25, 6.28) * mm, v(-1.15, 6.26) * mm], "startDerivative": vector(0.15, -0.13) * mm, "endDerivative": vector(0.2, -0.02) * mm});
            skFitSpline(sketch, "E206", {"points": [v(-0.32, 6.17) * mm, v(-0.24, 6.17) * mm, v(-0.16, 6.17) * mm], "startDerivative": vector(0.17, 0) * mm, "endDerivative": vector(0.15, 0) * mm});
            skFitSpline(sketch, "E207", {"points": [v(-0.16, 7.35) * mm, v(-0.19, 7.34) * mm, v(-0.27, 7.35) * mm], "startDerivative": vector(-0.06, -0.02) * mm, "endDerivative": vector(-0.15, 0.02) * mm});
            skFitSpline(sketch, "E208", {"points": [v(-0.8, 7.39) * mm, v(-0.86, 7.41) * mm, v(-0.91, 7.48) * mm], "startDerivative": vector(-0.12, 0.05) * mm, "endDerivative": vector(-0.1, 0.13) * mm});
            skFitSpline(sketch, "E209", {"points": [v(-8.87, 13.2) * mm, v(-8.8, 13.28) * mm, v(-8.68, 13.32) * mm, v(-8.59, 13.33) * mm], "startDerivative": vector(0.18, 0.27) * mm, "endDerivative": vector(0.29, 0) * mm});
            skFitSpline(sketch, "E210", {"points": [v(1.18, 13.2) * mm, v(1.15, 13.28) * mm, v(1.13, 13.33) * mm], "startDerivative": vector(-0.05, 0.15) * mm, "endDerivative": vector(-0.04, 0.1) * mm});
            skFitSpline(sketch, "E211", {"points": [v(3.7, 8.58) * mm, v(3.72, 8.52) * mm, v(3.72, 8.45) * mm, v(3.7, 8.4) * mm, v(3.67, 8.37) * mm, v(3.59, 8.32) * mm], "startDerivative": vector(0.07, -0.32) * mm, "endDerivative": vector(-0.37, -0.23) * mm});
            skFitSpline(sketch, "E212", {"points": [v(2.39, 8.75) * mm, v(2.43, 8.78) * mm, v(2.45, 8.82) * mm, v(2.45, 8.86) * mm, v(2.43, 8.95) * mm], "startDerivative": vector(0.2, 0.13) * mm, "endDerivative": vector(-0.1, 0.32) * mm});
            skFitSpline(sketch, "E213", {"points": [v(-5.71, 3.28) * mm, v(-5.77, 3.28) * mm, v(-5.83, 3.29) * mm, v(-5.86, 3.31) * mm, v(-5.9, 3.35) * mm, v(-5.9, 3.38) * mm, v(-5.9, 3.43) * mm, v(-5.9, 3.46) * mm, v(-5.9, 3.48) * mm], "startDerivative": vector(-0.4, 0) * mm, "endDerivative": vector(0.04, 0.24) * mm});
            skFitSpline(sketch, "E214", {"points": [v(-3.4, 3.4) * mm, v(-3.41, 3.4) * mm, v(-3.42, 3.42) * mm, v(-3.43, 3.43) * mm, v(-3.45, 3.44) * mm, v(-3.47, 3.44) * mm, v(-3.52, 3.44) * mm], "startDerivative": vector(-0.02, 0.12) * mm, "endDerivative": vector(-0.22, -0.02) * mm});
            skFitSpline(sketch, "E215", {"points": [v(-3.42, 2.63) * mm, v(-3.42, 2.65) * mm, v(-3.42, 2.7) * mm], "startDerivative": vector(-0.02, 0.05) * mm, "endDerivative": vector(0, 0.08) * mm});
            skFitSpline(sketch, "E216", {"points": [v(-0.63, -0.9) * mm, v(-0.65, -0.93) * mm, v(-0.7, -0.92) * mm, v(-0.73, -0.9) * mm, v(-0.76, -0.86) * mm], "startDerivative": vector(-0.1, -0.1) * mm, "endDerivative": vector(-0.12, 0.19) * mm});
            skFitSpline(sketch, "E217", {"points": [v(-8.87, -4.03) * mm, v(-8.87, -4.06) * mm, v(-8.86, -4.1) * mm, v(-8.83, -4.14) * mm, v(-8.8, -4.16) * mm, v(-8.77, -4.17) * mm, v(-8.75, -4.17) * mm], "startDerivative": vector(-0.01, -0.18) * mm, "endDerivative": vector(0.15, 0.01) * mm});
            skFitSpline(sketch, "E218", {"points": [v(7.58, -4.09) * mm, v(7.57, -4.15) * mm, v(7.5, -4.17) * mm], "startDerivative": vector(-0.01, -0.15) * mm, "endDerivative": vector(-0.16, -0.02) * mm});
            skFitSpline(sketch, "E219", {"points": [v(7.58, 2.37) * mm, v(7.58, 2.46) * mm, v(7.54, 2.56) * mm], "startDerivative": vector(0.02, 0.2) * mm, "endDerivative": vector(-0.1, 0.2) * mm});
            skFitSpline(sketch, "E220", {"points": [v(-6.36, 8.56) * mm, v(-6.41, 8.7) * mm, v(-6.36, 8.84) * mm], "startDerivative": vector(-0.15, 0.28) * mm, "endDerivative": vector(0.15, 0.27) * mm});
            skFitSpline(sketch, "E221", {"points": [v(-3.24, 10.14) * mm, v(-3.15, 10.16) * mm, v(-3.08, 10.14) * mm], "startDerivative": vector(0.18, 0.06) * mm, "endDerivative": vector(0.15, -0.07) * mm});
            skLineSegment(sketch, "E222", {"start": v(-10.25, -6.76) * mm, "end": v(-10.33, -7.57) * mm});
            skLineSegment(sketch, "E223", {"start": v(-10.33, -7.57) * mm, "end": v(-11.73, -7.43) * mm});
            skLineSegment(sketch, "E224", {"start": v(-11.73, -7.43) * mm, "end": v(-11.93, -8.86) * mm});
            skLineSegment(sketch, "E225", {"start": v(-11.93, -8.86) * mm, "end": v(-10.65, -9.04) * mm});
            skLineSegment(sketch, "E226", {"start": v(-10.65, -9.04) * mm, "end": v(-10.7, -9.62) * mm});
            skLineSegment(sketch, "E227", {"start": v(-10.7, -9.62) * mm, "end": v(-11.98, -9.52) * mm});
            skLineSegment(sketch, "E228", {"start": v(-11.98, -9.52) * mm, "end": v(-12.13, -11.24) * mm});
            skLineSegment(sketch, "E229", {"start": v(-12.13, -11.24) * mm, "end": v(-10.64, -11.37) * mm});
            skLineSegment(sketch, "E230", {"start": v(-10.64, -11.37) * mm, "end": v(-10.64, -11.96) * mm});
            skLineSegment(sketch, "E231", {"start": v(-10.64, -11.96) * mm, "end": v(-13.96, -11.72) * mm});
            skLineSegment(sketch, "E232", {"start": v(-13.96, -11.72) * mm, "end": v(-13.57, -6.37) * mm});
            skLineSegment(sketch, "E233", {"start": v(-13.57, -6.37) * mm, "end": v(-10.25, -6.76) * mm});
            skLineSegment(sketch, "E234", {"start": v(-9.22, -5.37) * mm, "end": v(-7.27, -5.6) * mm});
            skLineSegment(sketch, "E235", {"start": v(-7.27, -5.6) * mm, "end": v(-8.45, -10.95) * mm});
            skLineSegment(sketch, "E236", {"start": v(-8.45, -10.95) * mm, "end": v(-10.01, -10.57) * mm});
            skLineSegment(sketch, "E237", {"start": v(-10.01, -10.57) * mm, "end": v(-9.22, -5.37) * mm});
            skLineSegment(sketch, "E238", {"start": v(-3.9, -7.75) * mm, "end": v(-3.93, -8.72) * mm});
            skLineSegment(sketch, "E239", {"start": v(-3.93, -8.72) * mm, "end": v(-4.6, -8.72) * mm});
            skFitSpline(sketch, "E240", {"points": [v(-4.93, -7.85) * mm, v(-4.88, -7.69) * mm, v(-4.75, -7.53) * mm, v(-4.57, -7.44) * mm, v(-4.32, -7.45) * mm, v(-4.1, -7.52) * mm, v(-3.98, -7.63) * mm, v(-3.9, -7.75) * mm], "startDerivative": vector(0.24, 1.24) * mm, "endDerivative": vector(0.53, -0.96) * mm});
            skLineSegment(sketch, "E241", {"start": v(-2.11, -9.53) * mm, "end": v(-4.66, -9.2) * mm});
            skLineSegment(sketch, "E242", {"start": v(-3.79, -9.92) * mm, "end": v(-2.3, -10.11) * mm});
            skFitSpline(sketch, "E243", {"points": [v(-2.3, -10.11) * mm, v(-2.34, -10.38) * mm, v(-2.41, -10.6) * mm, v(-2.5, -10.82) * mm, v(-2.64, -11.02) * mm, v(-2.82, -11.21) * mm, v(-3.09, -11.37) * mm, v(-3.45, -11.46) * mm, v(-3.9, -11.51) * mm, v(-4.43, -11.51) * mm, v(-5, -11.5) * mm, v(-5.5, -11.43) * mm, v(-5.98, -11.26) * mm, v(-6.24, -11.1) * mm, v(-6.48, -10.9) * mm, v(-6.67, -10.57) * mm, v(-6.82, -10.11) * mm, v(-6.88, -9.54) * mm, v(-6.85, -9) * mm, v(-6.65, -8.16) * mm, v(-6.42, -7.74) * mm, v(-6.1, -7.44) * mm, v(-5.69, -7.21) * mm, v(-5.16, -7.05) * mm, v(-4.46, -7) * mm, v(-3.7, -7.1) * mm, v(-3.06, -7.3) * mm, v(-2.6, -7.6) * mm, v(-2.3, -7.93) * mm, v(-2.14, -8.3) * mm, v(-2.09, -8.64) * mm, v(-2.07, -9.03) * mm, v(-2.11, -9.53) * mm], "startDerivative": vector(-0.95, -11.32) * mm, "endDerivative": vector(-1.59, -15.64) * mm});
            skLineSegment(sketch, "E244", {"start": v(0.9, -11.07) * mm, "end": v(-0.73, -11.42) * mm});
            skLineSegment(sketch, "E245", {"start": v(-0.73, -11.42) * mm, "end": v(-1.9, -6.05) * mm});
            skLineSegment(sketch, "E246", {"start": v(-1.9, -6.05) * mm, "end": v(1.57, -5.55) * mm});
            skLineSegment(sketch, "E247", {"start": v(1.57, -5.55) * mm, "end": v(1.68, -6.35) * mm});
            skLineSegment(sketch, "E248", {"start": v(1.68, -6.35) * mm, "end": v(0.19, -6.64) * mm});
            skLineSegment(sketch, "E249", {"start": v(0.19, -6.64) * mm, "end": v(0.4, -8.1) * mm});
            skLineSegment(sketch, "E250", {"start": v(0.4, -8.1) * mm, "end": v(1.7, -7.9) * mm});
            skLineSegment(sketch, "E251", {"start": v(1.7, -7.9) * mm, "end": v(1.79, -8.46) * mm});
            skLineSegment(sketch, "E252", {"start": v(1.79, -8.46) * mm, "end": v(0.55, -8.7) * mm});
            skLineSegment(sketch, "E253", {"start": v(0.55, -8.7) * mm, "end": v(0.9, -11.07) * mm});
            skLineSegment(sketch, "E254", {"start": v(7.25, -11.07) * mm, "end": v(5.47, -11.4) * mm});
            skLineSegment(sketch, "E255", {"start": v(5.47, -11.4) * mm, "end": v(5.4, -11.18) * mm});
            skLineSegment(sketch, "E256", {"start": v(7.25, -11.07) * mm, "end": v(6.61, -6.64) * mm});
            skLineSegment(sketch, "E257", {"start": v(6.61, -6.64) * mm, "end": v(4.67, -7.06) * mm});
            skLineSegment(sketch, "E258", {"start": v(4.67, -7.06) * mm, "end": v(5.34, -10.47) * mm});
            skLineSegment(sketch, "E259", {"start": v(4.29, -10.8) * mm, "end": v(3.64, -7.43) * mm});
            skLineSegment(sketch, "E260", {"start": v(3.64, -7.43) * mm, "end": v(2.04, -7.65) * mm});
            skLineSegment(sketch, "E261", {"start": v(2.04, -7.65) * mm, "end": v(2.67, -11.2) * mm});
            skFitSpline(sketch, "E262", {"points": [v(2.67, -11.2) * mm, v(2.75, -11.41) * mm, v(2.94, -11.59) * mm, v(3.2, -11.7) * mm, v(3.53, -11.73) * mm, v(3.96, -11.7) * mm, v(4.34, -11.63) * mm, v(4.65, -11.51) * mm, v(4.94, -11.38) * mm, v(5.14, -11.29) * mm, v(5.27, -11.2) * mm, v(5.4, -11.18) * mm], "startDerivative": vector(0.77, -2.56) * mm, "endDerivative": vector(2.11, 0.24) * mm});
            skFitSpline(sketch, "E263", {"points": [v(5.34, -10.47) * mm, v(5.34, -10.62) * mm, v(5.25, -10.75) * mm, v(5.13, -10.86) * mm, v(4.94, -10.96) * mm, v(4.78, -11) * mm, v(4.6, -11.01) * mm, v(4.48, -10.98) * mm, v(4.38, -10.93) * mm, v(4.29, -10.8) * mm], "startDerivative": vector(0.2, -1.45) * mm, "endDerivative": vector(-0.8, 1.2) * mm});
            skLineSegment(sketch, "E264", {"start": v(9.82, -10.84) * mm, "end": v(8.22, -11.14) * mm});
            skLineSegment(sketch, "E265", {"start": v(8.22, -11.14) * mm, "end": v(7.37, -6.92) * mm});
            skLineSegment(sketch, "E266", {"start": v(7.37, -6.92) * mm, "end": v(9.29, -6.44) * mm});
            skLineSegment(sketch, "E267", {"start": v(9.29, -6.44) * mm, "end": v(9.32, -6.75) * mm});
            skLineSegment(sketch, "E268", {"start": v(9.25, -7.48) * mm, "end": v(9.82, -10.84) * mm});
            skLineSegment(sketch, "E269", {"start": v(10.93, -10.62) * mm, "end": v(10.33, -7.25) * mm});
            skLineSegment(sketch, "E270", {"start": v(10.93, -10.62) * mm, "end": v(12.65, -10.42) * mm});
            skLineSegment(sketch, "E271", {"start": v(12.65, -10.42) * mm, "end": v(12.02, -6.68) * mm});
            skPoint(sketch, "E272.1.internal.snap0", {"position": v(9.3, -6.6) * mm});
            skFitSpline(sketch, "E272", {"points": [v(9.25, -7.48) * mm, v(9.3, -7.3) * mm, v(9.42, -7.13) * mm, v(9.61, -7.01) * mm, v(9.85, -6.97) * mm, v(10.08, -7) * mm, v(10.19, -7.05) * mm, v(10.28, -7.12) * mm, v(10.33, -7.25) * mm], "startDerivative": vector(0.35, 1.5) * mm, "endDerivative": vector(0.4, -1.27) * mm});
            skFitSpline(sketch, "E273", {"points": [v(9.32, -6.75) * mm, v(9.5, -6.58) * mm, v(9.66, -6.45) * mm, v(9.97, -6.32) * mm, v(10.36, -6.2) * mm, v(10.78, -6.14) * mm, v(11.18, -6.15) * mm, v(11.53, -6.2) * mm, v(11.77, -6.3) * mm, v(11.91, -6.45) * mm, v(11.97, -6.56) * mm, v(12.02, -6.68) * mm], "startDerivative": vector(2, 2.1) * mm, "endDerivative": vector(0.8, -1.94) * mm});
            skFitSpline(sketch, "E274", {"points": [v(-4.84, -9.19) * mm, v(-4.93, -9.36) * mm, v(-5, -9.6) * mm, v(-5.08, -9.9) * mm, v(-5.1, -10.17) * mm, v(-5.11, -10.48) * mm, v(-5.05, -10.8) * mm, v(-4.87, -11.01) * mm, v(-4.65, -11.13) * mm, v(-4.42, -11.14) * mm, v(-4.23, -11.05) * mm, v(-4.09, -10.9) * mm, v(-3.96, -10.68) * mm, v(-3.87, -10.45) * mm, v(-3.82, -10.23) * mm, v(-3.79, -9.92) * mm], "startDerivative": vector(-1.74, -2.77) * mm, "endDerivative": vector(0.4, 4.42) * mm});
            skFitSpline(sketch, "E275", {"points": [v(-0.28, 4.7) * mm, v(-0.3, 4.78) * mm, v(-0.28, 4.87) * mm, v(-0.19, 4.94) * mm], "startDerivative": vector(-0.1, 0.25) * mm, "endDerivative": vector(0.3, 0.19) * mm});
            skLineSegment(sketch, "E276", {"start": v(8.16, 17.68) * mm, "end": v(14.27, 11.57) * mm, "construction": true});
            skCircle(sketch, "E277", {"center": v(11.21, 14.63) * mm, "radius": 1.5 * mm});
            skLineSegment(sketch, "E278.bottom", {"start": v(-13.73, 18.68) * mm, "end": v(12.27, 18.68) * mm});
            skLineSegment(sketch, "E278.top", {"start": v(-13.73, -13.32) * mm, "end": v(12.27, -13.32) * mm});
            skLineSegment(sketch, "E278.left", {"start": v(-16.73, 15.68) * mm, "end": v(-16.73, -10.32) * mm});
            skLineSegment(sketch, "E278.right", {"start": v(15.27, 15.68) * mm, "end": v(15.27, -10.32) * mm});
            skLineSegment(sketch, "E279", {"start": v(-16.73, 2.68) * mm, "end": v(15.27, 2.68) * mm, "construction": true});
            skLineSegment(sketch, "E280", {"start": v(-0.73, 18.68) * mm, "end": v(-0.73, -13.32) * mm, "construction": true});
            skLineSegment(sketch, "E281", {"start": v(-0.73, 2.68) * mm, "end": v(-0.73, -13.32) * mm, "construction": true});
            skLineSegment(sketch, "E282", {"start": v(-0.73, -13.32) * mm, "end": v(-0.73, 2.68) * mm, "construction": true});
            skLineSegment(sketch, "E283", {"start": v(-0.73, 18.68) * mm, "end": v(-0.73, 2.68) * mm, "construction": true});
            skPoint(sketch, "E284.visualSharp", {"position": v(-16.73, 18.68) * mm});
            skArc(sketch, "E284.filletArc", {"start": v(-13.73, 18.68) * mm, "mid": v(-15.85, 17.8) * mm, "end": v(-16.73, 15.68) * mm});
            skPoint(sketch, "E285.visualSharp", {"position": v(15.27, 18.68) * mm});
            skArc(sketch, "E285.filletArc", {"start": v(15.27, 15.68) * mm, "mid": v(14.39, 17.8) * mm, "end": v(12.27, 18.68) * mm});
            skPoint(sketch, "E286.visualSharp", {"position": v(15.27, -13.32) * mm});
            skArc(sketch, "E286.filletArc", {"start": v(12.27, -13.32) * mm, "mid": v(14.39, -12.44) * mm, "end": v(15.27, -10.32) * mm});
            skPoint(sketch, "E287.visualSharp", {"position": v(-16.73, -13.32) * mm});
            skArc(sketch, "E287.filletArc", {"start": v(-16.73, -10.32) * mm, "mid": v(-15.85, -12.44) * mm, "end": v(-13.73, -13.32) * mm});
            skLineSegment(sketch, "E288", {"start": v(-4.92, -7.8) * mm, "end": v(-5.1, -10.17) * mm});
            skLineSegment(sketch, "E289", {"start": v(-4.6, -8.72) * mm, "end": v(-4.66, -9.2) * mm});
            skSolve(sketch);
        }
        {
            var Q0;
            Q0=qSketchRegion(id+"F3",true);
            var Q1;
            {var subQ0=sQuery(id+"F3.wireOp",EDGE,"E277");var subQ1=makeQuery(id+"F1.opExtrude","CAP_EDGE",EDGE,{"disambiguationData":[OSD([sQuery(id+"F0.wireOp",EDGE,"E133.top")])],"isStart":false});var subQ2=makeQuery(id+"F3.imprint","INTERSECT",VERTEX,{"disambiguationData":[OD(0.0)],"derivedFrom":[subQ1,subQ0]});Q1=makeQuery(id+"F3.imprint","IMPRINT",FACE,{"disambiguationData":[TD([[makeQuery(id+"F3.imprint","IMPRINT",EDGE,{"disambiguationData":[TD([[subQ2,1.0]])],"derivedFrom":subQ0}),1.0]])]});}
            var Q2;
            {var subQ0=sQuery(id+"F3.wireOp",EDGE,"E277");var subQ1=makeQuery(id+"F1.opExtrude","CAP_EDGE",EDGE,{"disambiguationData":[OSD([sQuery(id+"F0.wireOp",EDGE,"E133.top")])],"isStart":false});var subQ2=makeQuery(id+"F3.imprint","INTERSECT",VERTEX,{"disambiguationData":[OD(0.0)],"derivedFrom":[subQ1,subQ0]});Q2=makeQuery(id+"F3.imprint","IMPRINT",FACE,{"disambiguationData":[TD([[makeQuery(id+"F3.imprint","IMPRINT",EDGE,{"disambiguationData":[TD([[subQ2,-1.0]])],"derivedFrom":subQ0}),1.0]])]});}
            extrude(context, id + "F4", {"entities" : qUnion([Q0, Q1, Q2]), "depth" : 1 * mm});
        }
        {
            var Q0;
            Q0=makeQuery(id+"F4.opExtrude","SWEPT_BODY",BODY,{"disambiguationData":[OSD([sQuery(id+"F3.wireOp",EDGE,"E148"),sQuery(id+"F3.wireOp",EDGE,"E149"),sQuery(id+"F3.wireOp",EDGE,"E150"),sQuery(id+"F3.wireOp",EDGE,"E151"),sQuery(id+"F3.wireOp",EDGE,"E152"),sQuery(id+"F3.wireOp",EDGE,"E153"),sQuery(id+"F3.wireOp",EDGE,"E154"),sQuery(id+"F3.wireOp",EDGE,"E155"),sQuery(id+"F3.wireOp",EDGE,"E156"),sQuery(id+"F3.wireOp",EDGE,"E157"),sQuery(id+"F3.wireOp",EDGE,"E158"),sQuery(id+"F3.wireOp",EDGE,"E159"),sQuery(id+"F3.wireOp",EDGE,"E160"),sQuery(id+"F3.wireOp",EDGE,"E161"),sQuery(id+"F3.wireOp",EDGE,"E162"),sQuery(id+"F3.wireOp",EDGE,"E163"),sQuery(id+"F3.wireOp",EDGE,"E164"),sQuery(id+"F3.wireOp",EDGE,"E165"),sQuery(id+"F3.wireOp",EDGE,"E166"),sQuery(id+"F3.wireOp",EDGE,"E167"),sQuery(id+"F3.wireOp",EDGE,"E168"),sQuery(id+"F3.wireOp",EDGE,"E169"),sQuery(id+"F3.wireOp",EDGE,"E170"),sQuery(id+"F3.wireOp",EDGE,"E171"),sQuery(id+"F3.wireOp",EDGE,"E172"),sQuery(id+"F3.wireOp",EDGE,"E173"),sQuery(id+"F3.wireOp",EDGE,"E174"),sQuery(id+"F3.wireOp",EDGE,"E175"),sQuery(id+"F3.wireOp",EDGE,"E176"),sQuery(id+"F3.wireOp",EDGE,"E177"),sQuery(id+"F3.wireOp",EDGE,"E178"),sQuery(id+"F3.wireOp",EDGE,"E179"),sQuery(id+"F3.wireOp",EDGE,"E180"),sQuery(id+"F3.wireOp",EDGE,"E181"),sQuery(id+"F3.wireOp",EDGE,"E182"),sQuery(id+"F3.wireOp",EDGE,"E183"),sQuery(id+"F3.wireOp",EDGE,"E184"),sQuery(id+"F3.wireOp",EDGE,"E185"),sQuery(id+"F3.wireOp",EDGE,"E186"),sQuery(id+"F3.wireOp",EDGE,"E187"),sQuery(id+"F3.wireOp",EDGE,"E188"),sQuery(id+"F3.wireOp",EDGE,"E189"),sQuery(id+"F3.wireOp",EDGE,"E190"),sQuery(id+"F3.wireOp",EDGE,"E191"),sQuery(id+"F3.wireOp",EDGE,"E192"),sQuery(id+"F3.wireOp",EDGE,"E193"),sQuery(id+"F3.wireOp",EDGE,"E194"),sQuery(id+"F3.wireOp",EDGE,"E195"),sQuery(id+"F3.wireOp",EDGE,"E196"),sQuery(id+"F3.wireOp",EDGE,"E197"),sQuery(id+"F3.wireOp",EDGE,"E198"),sQuery(id+"F3.wireOp",EDGE,"E199"),sQuery(id+"F3.wireOp",EDGE,"E200"),sQuery(id+"F3.wireOp",EDGE,"E201"),sQuery(id+"F3.wireOp",EDGE,"E202"),sQuery(id+"F3.wireOp",EDGE,"E203"),sQuery(id+"F3.wireOp",EDGE,"E204"),sQuery(id+"F3.wireOp",EDGE,"E205"),sQuery(id+"F3.wireOp",EDGE,"E206"),sQuery(id+"F3.wireOp",EDGE,"E207"),sQuery(id+"F3.wireOp",EDGE,"E208"),sQuery(id+"F3.wireOp",EDGE,"E209"),sQuery(id+"F3.wireOp",EDGE,"E210"),sQuery(id+"F3.wireOp",EDGE,"E211"),sQuery(id+"F3.wireOp",EDGE,"E212"),sQuery(id+"F3.wireOp",EDGE,"E213"),sQuery(id+"F3.wireOp",EDGE,"E214"),sQuery(id+"F3.wireOp",EDGE,"E215"),sQuery(id+"F3.wireOp",EDGE,"E216"),sQuery(id+"F3.wireOp",EDGE,"E217"),sQuery(id+"F3.wireOp",EDGE,"E218"),sQuery(id+"F3.wireOp",EDGE,"E219"),sQuery(id+"F3.wireOp",EDGE,"E220"),sQuery(id+"F3.wireOp",EDGE,"E221"),sQuery(id+"F3.wireOp",EDGE,"E222"),sQuery(id+"F3.wireOp",EDGE,"E223"),sQuery(id+"F3.wireOp",EDGE,"E224"),sQuery(id+"F3.wireOp",EDGE,"E225"),sQuery(id+"F3.wireOp",EDGE,"E226"),sQuery(id+"F3.wireOp",EDGE,"E227"),sQuery(id+"F3.wireOp",EDGE,"E228"),sQuery(id+"F3.wireOp",EDGE,"E229"),sQuery(id+"F3.wireOp",EDGE,"E230"),sQuery(id+"F3.wireOp",EDGE,"E231"),sQuery(id+"F3.wireOp",EDGE,"E232"),sQuery(id+"F3.wireOp",EDGE,"E233"),sQuery(id+"F3.wireOp",EDGE,"E234"),sQuery(id+"F3.wireOp",EDGE,"E235"),sQuery(id+"F3.wireOp",EDGE,"E236"),sQuery(id+"F3.wireOp",EDGE,"E237"),sQuery(id+"F3.wireOp",EDGE,"E238"),sQuery(id+"F3.wireOp",EDGE,"E239"),sQuery(id+"F3.wireOp",EDGE,"E240"),sQuery(id+"F3.wireOp",EDGE,"E241"),sQuery(id+"F3.wireOp",EDGE,"E242"),sQuery(id+"F3.wireOp",EDGE,"E243"),sQuery(id+"F3.wireOp",EDGE,"E244"),sQuery(id+"F3.wireOp",EDGE,"E245"),sQuery(id+"F3.wireOp",EDGE,"E246"),sQuery(id+"F3.wireOp",EDGE,"E247"),sQuery(id+"F3.wireOp",EDGE,"E248"),sQuery(id+"F3.wireOp",EDGE,"E249"),sQuery(id+"F3.wireOp",EDGE,"E250"),sQuery(id+"F3.wireOp",EDGE,"E251"),sQuery(id+"F3.wireOp",EDGE,"E252"),sQuery(id+"F3.wireOp",EDGE,"E253"),sQuery(id+"F3.wireOp",EDGE,"E254"),sQuery(id+"F3.wireOp",EDGE,"E255"),sQuery(id+"F3.wireOp",EDGE,"E256"),sQuery(id+"F3.wireOp",EDGE,"E257"),sQuery(id+"F3.wireOp",EDGE,"E258"),sQuery(id+"F3.wireOp",EDGE,"E259"),sQuery(id+"F3.wireOp",EDGE,"E260"),sQuery(id+"F3.wireOp",EDGE,"E261"),sQuery(id+"F3.wireOp",EDGE,"E262"),sQuery(id+"F3.wireOp",EDGE,"E263"),sQuery(id+"F3.wireOp",EDGE,"E264"),sQuery(id+"F3.wireOp",EDGE,"E265"),sQuery(id+"F3.wireOp",EDGE,"E266"),sQuery(id+"F3.wireOp",EDGE,"E267"),sQuery(id+"F3.wireOp",EDGE,"E268"),sQuery(id+"F3.wireOp",EDGE,"E269"),sQuery(id+"F3.wireOp",EDGE,"E270"),sQuery(id+"F3.wireOp",EDGE,"E271"),sQuery(id+"F3.wireOp",EDGE,"E272"),sQuery(id+"F3.wireOp",EDGE,"E273"),sQuery(id+"F3.wireOp",EDGE,"E274"),sQuery(id+"F3.wireOp",EDGE,"E275"),sQuery(id+"F3.wireOp",EDGE,"E278.bottom"),sQuery(id+"F3.wireOp",EDGE,"E278.top"),sQuery(id+"F3.wireOp",EDGE,"E278.left"),sQuery(id+"F3.wireOp",EDGE,"E278.right"),sQuery(id+"F3.wireOp",EDGE,"E284.filletArc"),sQuery(id+"F3.wireOp",EDGE,"E285.filletArc"),sQuery(id+"F3.wireOp",EDGE,"E286.filletArc"),sQuery(id+"F3.wireOp",EDGE,"E287.filletArc"),sQuery(id+"F3.wireOp",EDGE,"E288"),sQuery(id+"F3.wireOp",EDGE,"E289")])]});
            var Q1;
            Q1=makeQuery(id+"F4.opExtrude","SWEPT_EDGE",EDGE,{"disambiguationData":[OSD([sQuery(id+"F3.wireOp",EDGE,"E278.top"),sQuery(id+"F3.wireOp",EDGE,"E286.filletArc")])]});
            transform(context, id + "F5", {"entities" : qUnion([Q0]), "transformType" : TransformType.ROTATION, "transformAxis" : qUnion([Q1]), "angle" : 180 * degree, "oppositeDirection" : true, "makeCopy" : false});
        }
        {
            var Q0;
            Q0=makeQuery(id+"F4.opExtrude","CAP_EDGE",EDGE,{"disambiguationData":[OSD([sQuery(id+"F3.wireOp",EDGE,"E286.filletArc")])],"isStart":true});
            cPoint(context, id + "F6", {"entities" : qUnion([Q0]), "parameter" : 0.5});
        }
        {
            var Q0;
            Q0=makeQuery(id+"F1.opExtrude","CAP_EDGE",EDGE,{"disambiguationData":[OSD([sQuery(id+"F0.wireOp",EDGE,"E142.filletArc")])],"isStart":false});
            cPoint(context, id + "F7", {"entities" : qUnion([Q0]), "parameter" : 0.5});
        }
        {
            var Q0;
            Q0=makeQuery(id+"F4.opExtrude","SWEPT_BODY",BODY,{"disambiguationData":[OSD([sQuery(id+"F3.wireOp",EDGE,"E148"),sQuery(id+"F3.wireOp",EDGE,"E149"),sQuery(id+"F3.wireOp",EDGE,"E150"),sQuery(id+"F3.wireOp",EDGE,"E151"),sQuery(id+"F3.wireOp",EDGE,"E152"),sQuery(id+"F3.wireOp",EDGE,"E153"),sQuery(id+"F3.wireOp",EDGE,"E154"),sQuery(id+"F3.wireOp",EDGE,"E155"),sQuery(id+"F3.wireOp",EDGE,"E156"),sQuery(id+"F3.wireOp",EDGE,"E157"),sQuery(id+"F3.wireOp",EDGE,"E158"),sQuery(id+"F3.wireOp",EDGE,"E159"),sQuery(id+"F3.wireOp",EDGE,"E160"),sQuery(id+"F3.wireOp",EDGE,"E161"),sQuery(id+"F3.wireOp",EDGE,"E162"),sQuery(id+"F3.wireOp",EDGE,"E163"),sQuery(id+"F3.wireOp",EDGE,"E164"),sQuery(id+"F3.wireOp",EDGE,"E165"),sQuery(id+"F3.wireOp",EDGE,"E166"),sQuery(id+"F3.wireOp",EDGE,"E167"),sQuery(id+"F3.wireOp",EDGE,"E168"),sQuery(id+"F3.wireOp",EDGE,"E169"),sQuery(id+"F3.wireOp",EDGE,"E170"),sQuery(id+"F3.wireOp",EDGE,"E171"),sQuery(id+"F3.wireOp",EDGE,"E172"),sQuery(id+"F3.wireOp",EDGE,"E173"),sQuery(id+"F3.wireOp",EDGE,"E174"),sQuery(id+"F3.wireOp",EDGE,"E175"),sQuery(id+"F3.wireOp",EDGE,"E176"),sQuery(id+"F3.wireOp",EDGE,"E177"),sQuery(id+"F3.wireOp",EDGE,"E178"),sQuery(id+"F3.wireOp",EDGE,"E179"),sQuery(id+"F3.wireOp",EDGE,"E180"),sQuery(id+"F3.wireOp",EDGE,"E181"),sQuery(id+"F3.wireOp",EDGE,"E182"),sQuery(id+"F3.wireOp",EDGE,"E183"),sQuery(id+"F3.wireOp",EDGE,"E184"),sQuery(id+"F3.wireOp",EDGE,"E185"),sQuery(id+"F3.wireOp",EDGE,"E186"),sQuery(id+"F3.wireOp",EDGE,"E187"),sQuery(id+"F3.wireOp",EDGE,"E188"),sQuery(id+"F3.wireOp",EDGE,"E189"),sQuery(id+"F3.wireOp",EDGE,"E190"),sQuery(id+"F3.wireOp",EDGE,"E191"),sQuery(id+"F3.wireOp",EDGE,"E192"),sQuery(id+"F3.wireOp",EDGE,"E193"),sQuery(id+"F3.wireOp",EDGE,"E194"),sQuery(id+"F3.wireOp",EDGE,"E195"),sQuery(id+"F3.wireOp",EDGE,"E196"),sQuery(id+"F3.wireOp",EDGE,"E197"),sQuery(id+"F3.wireOp",EDGE,"E198"),sQuery(id+"F3.wireOp",EDGE,"E199"),sQuery(id+"F3.wireOp",EDGE,"E200"),sQuery(id+"F3.wireOp",EDGE,"E201"),sQuery(id+"F3.wireOp",EDGE,"E202"),sQuery(id+"F3.wireOp",EDGE,"E203"),sQuery(id+"F3.wireOp",EDGE,"E204"),sQuery(id+"F3.wireOp",EDGE,"E205"),sQuery(id+"F3.wireOp",EDGE,"E206"),sQuery(id+"F3.wireOp",EDGE,"E207"),sQuery(id+"F3.wireOp",EDGE,"E208"),sQuery(id+"F3.wireOp",EDGE,"E209"),sQuery(id+"F3.wireOp",EDGE,"E210"),sQuery(id+"F3.wireOp",EDGE,"E211"),sQuery(id+"F3.wireOp",EDGE,"E212"),sQuery(id+"F3.wireOp",EDGE,"E213"),sQuery(id+"F3.wireOp",EDGE,"E214"),sQuery(id+"F3.wireOp",EDGE,"E215"),sQuery(id+"F3.wireOp",EDGE,"E216"),sQuery(id+"F3.wireOp",EDGE,"E217"),sQuery(id+"F3.wireOp",EDGE,"E218"),sQuery(id+"F3.wireOp",EDGE,"E219"),sQuery(id+"F3.wireOp",EDGE,"E220"),sQuery(id+"F3.wireOp",EDGE,"E221"),sQuery(id+"F3.wireOp",EDGE,"E222"),sQuery(id+"F3.wireOp",EDGE,"E223"),sQuery(id+"F3.wireOp",EDGE,"E224"),sQuery(id+"F3.wireOp",EDGE,"E225"),sQuery(id+"F3.wireOp",EDGE,"E226"),sQuery(id+"F3.wireOp",EDGE,"E227"),sQuery(id+"F3.wireOp",EDGE,"E228"),sQuery(id+"F3.wireOp",EDGE,"E229"),sQuery(id+"F3.wireOp",EDGE,"E230"),sQuery(id+"F3.wireOp",EDGE,"E231"),sQuery(id+"F3.wireOp",EDGE,"E232"),sQuery(id+"F3.wireOp",EDGE,"E233"),sQuery(id+"F3.wireOp",EDGE,"E234"),sQuery(id+"F3.wireOp",EDGE,"E235"),sQuery(id+"F3.wireOp",EDGE,"E236"),sQuery(id+"F3.wireOp",EDGE,"E237"),sQuery(id+"F3.wireOp",EDGE,"E238"),sQuery(id+"F3.wireOp",EDGE,"E239"),sQuery(id+"F3.wireOp",EDGE,"E240"),sQuery(id+"F3.wireOp",EDGE,"E241"),sQuery(id+"F3.wireOp",EDGE,"E242"),sQuery(id+"F3.wireOp",EDGE,"E243"),sQuery(id+"F3.wireOp",EDGE,"E244"),sQuery(id+"F3.wireOp",EDGE,"E245"),sQuery(id+"F3.wireOp",EDGE,"E246"),sQuery(id+"F3.wireOp",EDGE,"E247"),sQuery(id+"F3.wireOp",EDGE,"E248"),sQuery(id+"F3.wireOp",EDGE,"E249"),sQuery(id+"F3.wireOp",EDGE,"E250"),sQuery(id+"F3.wireOp",EDGE,"E251"),sQuery(id+"F3.wireOp",EDGE,"E252"),sQuery(id+"F3.wireOp",EDGE,"E253"),sQuery(id+"F3.wireOp",EDGE,"E254"),sQuery(id+"F3.wireOp",EDGE,"E255"),sQuery(id+"F3.wireOp",EDGE,"E256"),sQuery(id+"F3.wireOp",EDGE,"E257"),sQuery(id+"F3.wireOp",EDGE,"E258"),sQuery(id+"F3.wireOp",EDGE,"E259"),sQuery(id+"F3.wireOp",EDGE,"E260"),sQuery(id+"F3.wireOp",EDGE,"E261"),sQuery(id+"F3.wireOp",EDGE,"E262"),sQuery(id+"F3.wireOp",EDGE,"E263"),sQuery(id+"F3.wireOp",EDGE,"E264"),sQuery(id+"F3.wireOp",EDGE,"E265"),sQuery(id+"F3.wireOp",EDGE,"E266"),sQuery(id+"F3.wireOp",EDGE,"E267"),sQuery(id+"F3.wireOp",EDGE,"E268"),sQuery(id+"F3.wireOp",EDGE,"E269"),sQuery(id+"F3.wireOp",EDGE,"E270"),sQuery(id+"F3.wireOp",EDGE,"E271"),sQuery(id+"F3.wireOp",EDGE,"E272"),sQuery(id+"F3.wireOp",EDGE,"E273"),sQuery(id+"F3.wireOp",EDGE,"E274"),sQuery(id+"F3.wireOp",EDGE,"E275"),sQuery(id+"F3.wireOp",EDGE,"E278.bottom"),sQuery(id+"F3.wireOp",EDGE,"E278.top"),sQuery(id+"F3.wireOp",EDGE,"E278.left"),sQuery(id+"F3.wireOp",EDGE,"E278.right"),sQuery(id+"F3.wireOp",EDGE,"E284.filletArc"),sQuery(id+"F3.wireOp",EDGE,"E285.filletArc"),sQuery(id+"F3.wireOp",EDGE,"E286.filletArc"),sQuery(id+"F3.wireOp",EDGE,"E287.filletArc"),sQuery(id+"F3.wireOp",EDGE,"E288"),sQuery(id+"F3.wireOp",EDGE,"E289")])]});
            var Q1;
            Q1=qCreatedBy(id+"F6",VERTEX);
            var Q2;
            Q2=qCreatedBy(id+"F7",VERTEX);
            transform(context, id + "F8", {"entities" : qUnion([Q0]), "transformType" : TransformType.TRANSLATION_ENTITY, "oppositeDirectionEntity" : false, "transformLine" : qUnion([Q1, Q2]), "makeCopy" : false});
        }
        {
            var Q0;
            Q0=makeQuery(id+"F0.imprint","IMPRINT",FACE,{"disambiguationData":[TD([[makeQuery(id+"F0.imprint","IMPRINT",EDGE,{"derivedFrom":sQuery(id+"F0.wireOp",EDGE,"E132")}),1.0]])]});
            var Q1;
            Q1=sQuery(id+"F0.wireOp",EDGE,"E132");
            extrude(context, id + "F9", {"entities" : qUnion([Q0]), "operationType" : NewBodyOperationType.REMOVE, "surfaceEntities" : qUnion([Q1]), "endBound" : BoundingType.THROUGH_ALL, "oppositeDirection" : true, "depth" : 25 * mm});
        }
        {
            var Q0;
            Q0=makeQuery(id+"F2.opExtrude","CAP_EDGE",EDGE,{"disambiguationData":[OSD([sQuery(id+"F0.wireOp",EDGE,"E132")])],"isStart":false});
            var Q1;
            Q1=makeQuery(id+"F9.boolean.opBoolean","INTERSECT",EDGE,{"derivedFrom":[makeQuery(id+"F4.opExtrude","CAP_FACE",FACE,{"disambiguationData":[OSD([sQuery(id+"F3.wireOp",EDGE,"E148"),sQuery(id+"F3.wireOp",EDGE,"E149"),sQuery(id+"F3.wireOp",EDGE,"E150"),sQuery(id+"F3.wireOp",EDGE,"E151"),sQuery(id+"F3.wireOp",EDGE,"E152"),sQuery(id+"F3.wireOp",EDGE,"E153"),sQuery(id+"F3.wireOp",EDGE,"E154"),sQuery(id+"F3.wireOp",EDGE,"E155"),sQuery(id+"F3.wireOp",EDGE,"E156"),sQuery(id+"F3.wireOp",EDGE,"E157"),sQuery(id+"F3.wireOp",EDGE,"E158"),sQuery(id+"F3.wireOp",EDGE,"E159"),sQuery(id+"F3.wireOp",EDGE,"E160"),sQuery(id+"F3.wireOp",EDGE,"E161"),sQuery(id+"F3.wireOp",EDGE,"E162"),sQuery(id+"F3.wireOp",EDGE,"E163"),sQuery(id+"F3.wireOp",EDGE,"E164"),sQuery(id+"F3.wireOp",EDGE,"E165"),sQuery(id+"F3.wireOp",EDGE,"E166"),sQuery(id+"F3.wireOp",EDGE,"E167"),sQuery(id+"F3.wireOp",EDGE,"E168"),sQuery(id+"F3.wireOp",EDGE,"E169"),sQuery(id+"F3.wireOp",EDGE,"E170"),sQuery(id+"F3.wireOp",EDGE,"E171"),sQuery(id+"F3.wireOp",EDGE,"E172"),sQuery(id+"F3.wireOp",EDGE,"E173"),sQuery(id+"F3.wireOp",EDGE,"E174"),sQuery(id+"F3.wireOp",EDGE,"E175"),sQuery(id+"F3.wireOp",EDGE,"E176"),sQuery(id+"F3.wireOp",EDGE,"E177"),sQuery(id+"F3.wireOp",EDGE,"E178"),sQuery(id+"F3.wireOp",EDGE,"E179"),sQuery(id+"F3.wireOp",EDGE,"E180"),sQuery(id+"F3.wireOp",EDGE,"E181"),sQuery(id+"F3.wireOp",EDGE,"E182"),sQuery(id+"F3.wireOp",EDGE,"E183"),sQuery(id+"F3.wireOp",EDGE,"E184"),sQuery(id+"F3.wireOp",EDGE,"E185"),sQuery(id+"F3.wireOp",EDGE,"E186"),sQuery(id+"F3.wireOp",EDGE,"E187"),sQuery(id+"F3.wireOp",EDGE,"E188"),sQuery(id+"F3.wireOp",EDGE,"E189"),sQuery(id+"F3.wireOp",EDGE,"E190"),sQuery(id+"F3.wireOp",EDGE,"E191"),sQuery(id+"F3.wireOp",EDGE,"E192"),sQuery(id+"F3.wireOp",EDGE,"E193"),sQuery(id+"F3.wireOp",EDGE,"E194"),sQuery(id+"F3.wireOp",EDGE,"E195"),sQuery(id+"F3.wireOp",EDGE,"E196"),sQuery(id+"F3.wireOp",EDGE,"E197"),sQuery(id+"F3.wireOp",EDGE,"E198"),sQuery(id+"F3.wireOp",EDGE,"E199"),sQuery(id+"F3.wireOp",EDGE,"E200"),sQuery(id+"F3.wireOp",EDGE,"E201"),sQuery(id+"F3.wireOp",EDGE,"E202"),sQuery(id+"F3.wireOp",EDGE,"E203"),sQuery(id+"F3.wireOp",EDGE,"E204"),sQuery(id+"F3.wireOp",EDGE,"E205"),sQuery(id+"F3.wireOp",EDGE,"E206"),sQuery(id+"F3.wireOp",EDGE,"E207"),sQuery(id+"F3.wireOp",EDGE,"E208"),sQuery(id+"F3.wireOp",EDGE,"E209"),sQuery(id+"F3.wireOp",EDGE,"E210"),sQuery(id+"F3.wireOp",EDGE,"E211"),sQuery(id+"F3.wireOp",EDGE,"E212"),sQuery(id+"F3.wireOp",EDGE,"E213"),sQuery(id+"F3.wireOp",EDGE,"E214"),sQuery(id+"F3.wireOp",EDGE,"E215"),sQuery(id+"F3.wireOp",EDGE,"E216"),sQuery(id+"F3.wireOp",EDGE,"E217"),sQuery(id+"F3.wireOp",EDGE,"E218"),sQuery(id+"F3.wireOp",EDGE,"E219"),sQuery(id+"F3.wireOp",EDGE,"E220"),sQuery(id+"F3.wireOp",EDGE,"E221"),sQuery(id+"F3.wireOp",EDGE,"E222"),sQuery(id+"F3.wireOp",EDGE,"E223"),sQuery(id+"F3.wireOp",EDGE,"E224"),sQuery(id+"F3.wireOp",EDGE,"E225"),sQuery(id+"F3.wireOp",EDGE,"E226"),sQuery(id+"F3.wireOp",EDGE,"E227"),sQuery(id+"F3.wireOp",EDGE,"E228"),sQuery(id+"F3.wireOp",EDGE,"E229"),sQuery(id+"F3.wireOp",EDGE,"E230"),sQuery(id+"F3.wireOp",EDGE,"E231"),sQuery(id+"F3.wireOp",EDGE,"E232"),sQuery(id+"F3.wireOp",EDGE,"E233"),sQuery(id+"F3.wireOp",EDGE,"E234"),sQuery(id+"F3.wireOp",EDGE,"E235"),sQuery(id+"F3.wireOp",EDGE,"E236"),sQuery(id+"F3.wireOp",EDGE,"E237"),sQuery(id+"F3.wireOp",EDGE,"E238"),sQuery(id+"F3.wireOp",EDGE,"E239"),sQuery(id+"F3.wireOp",EDGE,"E240"),sQuery(id+"F3.wireOp",EDGE,"E241"),sQuery(id+"F3.wireOp",EDGE,"E242"),sQuery(id+"F3.wireOp",EDGE,"E243"),sQuery(id+"F3.wireOp",EDGE,"E244"),sQuery(id+"F3.wireOp",EDGE,"E245"),sQuery(id+"F3.wireOp",EDGE,"E246"),sQuery(id+"F3.wireOp",EDGE,"E247"),sQuery(id+"F3.wireOp",EDGE,"E248"),sQuery(id+"F3.wireOp",EDGE,"E249"),sQuery(id+"F3.wireOp",EDGE,"E250"),sQuery(id+"F3.wireOp",EDGE,"E251"),sQuery(id+"F3.wireOp",EDGE,"E252"),sQuery(id+"F3.wireOp",EDGE,"E253"),sQuery(id+"F3.wireOp",EDGE,"E254"),sQuery(id+"F3.wireOp",EDGE,"E255"),sQuery(id+"F3.wireOp",EDGE,"E256"),sQuery(id+"F3.wireOp",EDGE,"E257"),sQuery(id+"F3.wireOp",EDGE,"E258"),sQuery(id+"F3.wireOp",EDGE,"E259"),sQuery(id+"F3.wireOp",EDGE,"E260"),sQuery(id+"F3.wireOp",EDGE,"E261"),sQuery(id+"F3.wireOp",EDGE,"E262"),sQuery(id+"F3.wireOp",EDGE,"E263"),sQuery(id+"F3.wireOp",EDGE,"E264"),sQuery(id+"F3.wireOp",EDGE,"E265"),sQuery(id+"F3.wireOp",EDGE,"E266"),sQuery(id+"F3.wireOp",EDGE,"E267"),sQuery(id+"F3.wireOp",EDGE,"E268"),sQuery(id+"F3.wireOp",EDGE,"E269"),sQuery(id+"F3.wireOp",EDGE,"E270"),sQuery(id+"F3.wireOp",EDGE,"E271"),sQuery(id+"F3.wireOp",EDGE,"E272"),sQuery(id+"F3.wireOp",EDGE,"E273"),sQuery(id+"F3.wireOp",EDGE,"E274"),sQuery(id+"F3.wireOp",EDGE,"E275"),sQuery(id+"F3.wireOp",EDGE,"E278.bottom"),sQuery(id+"F3.wireOp",EDGE,"E278.top"),sQuery(id+"F3.wireOp",EDGE,"E278.left"),sQuery(id+"F3.wireOp",EDGE,"E278.right"),sQuery(id+"F3.wireOp",EDGE,"E284.filletArc"),sQuery(id+"F3.wireOp",EDGE,"E285.filletArc"),sQuery(id+"F3.wireOp",EDGE,"E286.filletArc"),sQuery(id+"F3.wireOp",EDGE,"E287.filletArc"),sQuery(id+"F3.wireOp",EDGE,"E288"),sQuery(id+"F3.wireOp",EDGE,"E289")])],"isStart":false}),makeQuery(id+"F9.opExtrude","SWEPT_FACE",FACE,{"disambiguationData":[OSD([sQuery(id+"F0.wireOp",EDGE,"E132")])]})]});
            var Q2;
            Q2=makeQuery(id+"F4.opExtrude","CAP_EDGE",EDGE,{"disambiguationData":[OSD([sQuery(id+"F3.wireOp",EDGE,"E278.bottom")])],"isStart":false});
            var Q3;
            Q3=makeQuery(id+"F2.opExtrude","CAP_EDGE",EDGE,{"disambiguationData":[OSD([sQuery(id+"F0.wireOp",EDGE,"E133.bottom")])],"isStart":false});
            fillet(context, id + "F10", {"entities" : qUnion([Q0, Q1, Q2, Q3]), "radius" : 1 * mm, "tangentPropagation" : true, "allowEdgeOverflow" : false});
        }
    });
